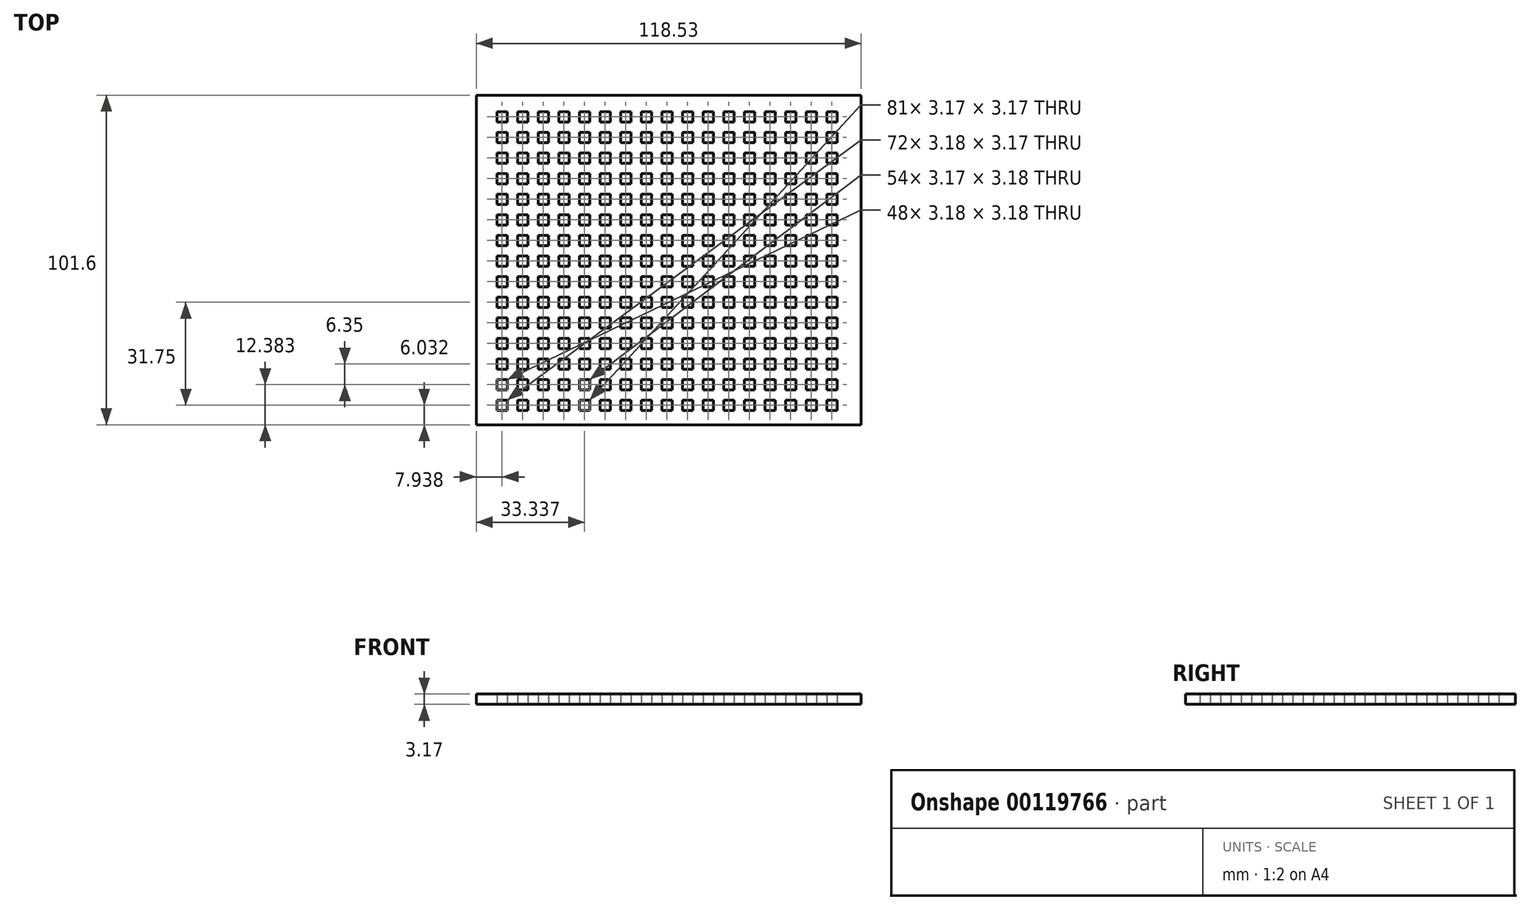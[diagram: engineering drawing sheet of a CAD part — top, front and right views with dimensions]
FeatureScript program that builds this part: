
annotation { "Feature Type Name" : "Feature", "Feature Type Description" : "" }
export const myFeature = defineFeature(function(context is Context, id is Id, definition is map)
    precondition{}
    {
        {
            assignVariable(context, id + "F0", {"name" : "thickness", "anyValue" : 3.17 * mm});
        }
        {
            var Q0;
            Q0=qCreatedBy(makeId("Top.planeOp"),FACE);
            var sketch = newSketch(context, id + "F1", { "sketchPlane" : qUnion([Q0])});
            skLineSegment(sketch, "E0.bottom", {"start": v(0, 0) * mm, "end": v(118.53, 0) * mm});
            skLineSegment(sketch, "E0.top", {"start": v(0, 101.6) * mm, "end": v(118.53, 101.6) * mm});
            skLineSegment(sketch, "E0.left", {"start": v(0, 0) * mm, "end": v(0, 101.6) * mm});
            skLineSegment(sketch, "E0.right", {"start": v(118.53, 0) * mm, "end": v(118.53, 101.6) * mm});
            skLineSegment(sketch, "E1.bottom", {"start": v(6.35, 93.35) * mm, "end": v(9.53, 93.35) * mm});
            skLineSegment(sketch, "E1.top", {"start": v(6.35, 96.52) * mm, "end": v(9.53, 96.52) * mm});
            skLineSegment(sketch, "E1.left", {"start": v(6.35, 93.35) * mm, "end": v(6.35, 96.52) * mm});
            skLineSegment(sketch, "E1.right", {"start": v(9.52, 93.35) * mm, "end": v(9.52, 96.52) * mm});
            skLineSegment(sketch, "E2.0.1.0", {"start": v(6.35, 90.17) * mm, "end": v(9.53, 90.17) * mm});
            skLineSegment(sketch, "E2.0.1.1", {"start": v(9.52, 87) * mm, "end": v(9.52, 90.17) * mm});
            skLineSegment(sketch, "E2.0.1.2", {"start": v(6.35, 87) * mm, "end": v(9.53, 87) * mm});
            skLineSegment(sketch, "E2.0.1.3", {"start": v(6.35, 87) * mm, "end": v(6.35, 90.17) * mm});
            skLineSegment(sketch, "E2.0.2.0", {"start": v(6.35, 83.82) * mm, "end": v(9.53, 83.82) * mm});
            skLineSegment(sketch, "E2.0.2.1", {"start": v(9.52, 80.65) * mm, "end": v(9.52, 83.82) * mm});
            skLineSegment(sketch, "E2.0.2.2", {"start": v(6.35, 80.65) * mm, "end": v(9.53, 80.65) * mm});
            skLineSegment(sketch, "E2.0.2.3", {"start": v(6.35, 80.65) * mm, "end": v(6.35, 83.82) * mm});
            skLineSegment(sketch, "E2.0.3.0", {"start": v(6.35, 77.47) * mm, "end": v(9.53, 77.47) * mm});
            skLineSegment(sketch, "E2.0.3.1", {"start": v(9.52, 74.3) * mm, "end": v(9.52, 77.47) * mm});
            skLineSegment(sketch, "E2.0.3.2", {"start": v(6.35, 74.3) * mm, "end": v(9.53, 74.3) * mm});
            skLineSegment(sketch, "E2.0.3.3", {"start": v(6.35, 74.3) * mm, "end": v(6.35, 77.47) * mm});
            skLineSegment(sketch, "E2.0.4.0", {"start": v(6.35, 71.12) * mm, "end": v(9.53, 71.12) * mm});
            skLineSegment(sketch, "E2.0.4.1", {"start": v(9.52, 67.95) * mm, "end": v(9.52, 71.12) * mm});
            skLineSegment(sketch, "E2.0.4.2", {"start": v(6.35, 67.95) * mm, "end": v(9.53, 67.95) * mm});
            skLineSegment(sketch, "E2.0.4.3", {"start": v(6.35, 67.95) * mm, "end": v(6.35, 71.12) * mm});
            skLineSegment(sketch, "E2.0.5.0", {"start": v(6.35, 64.77) * mm, "end": v(9.53, 64.77) * mm});
            skLineSegment(sketch, "E2.0.5.1", {"start": v(9.52, 61.6) * mm, "end": v(9.52, 64.77) * mm});
            skLineSegment(sketch, "E2.0.5.2", {"start": v(6.35, 61.6) * mm, "end": v(9.53, 61.6) * mm});
            skLineSegment(sketch, "E2.0.5.3", {"start": v(6.35, 61.6) * mm, "end": v(6.35, 64.77) * mm});
            skLineSegment(sketch, "E2.0.6.0", {"start": v(6.35, 58.42) * mm, "end": v(9.53, 58.42) * mm});
            skLineSegment(sketch, "E2.0.6.1", {"start": v(9.52, 55.25) * mm, "end": v(9.52, 58.42) * mm});
            skLineSegment(sketch, "E2.0.6.2", {"start": v(6.35, 55.25) * mm, "end": v(9.53, 55.25) * mm});
            skLineSegment(sketch, "E2.0.6.3", {"start": v(6.35, 55.25) * mm, "end": v(6.35, 58.42) * mm});
            skLineSegment(sketch, "E2.0.7.0", {"start": v(6.35, 52.07) * mm, "end": v(9.53, 52.07) * mm});
            skLineSegment(sketch, "E2.0.7.1", {"start": v(9.52, 48.9) * mm, "end": v(9.52, 52.07) * mm});
            skLineSegment(sketch, "E2.0.7.2", {"start": v(6.35, 48.9) * mm, "end": v(9.53, 48.9) * mm});
            skLineSegment(sketch, "E2.0.7.3", {"start": v(6.35, 48.9) * mm, "end": v(6.35, 52.07) * mm});
            skLineSegment(sketch, "E2.0.8.0", {"start": v(6.35, 45.72) * mm, "end": v(9.53, 45.72) * mm});
            skLineSegment(sketch, "E2.0.8.1", {"start": v(9.52, 42.55) * mm, "end": v(9.52, 45.72) * mm});
            skLineSegment(sketch, "E2.0.8.2", {"start": v(6.35, 42.55) * mm, "end": v(9.53, 42.55) * mm});
            skLineSegment(sketch, "E2.0.8.3", {"start": v(6.35, 42.55) * mm, "end": v(6.35, 45.72) * mm});
            skLineSegment(sketch, "E2.0.9.0", {"start": v(6.35, 39.37) * mm, "end": v(9.53, 39.37) * mm});
            skLineSegment(sketch, "E2.0.9.1", {"start": v(9.52, 36.2) * mm, "end": v(9.52, 39.37) * mm});
            skLineSegment(sketch, "E2.0.9.2", {"start": v(6.35, 36.2) * mm, "end": v(9.53, 36.2) * mm});
            skLineSegment(sketch, "E2.0.9.3", {"start": v(6.35, 36.2) * mm, "end": v(6.35, 39.37) * mm});
            skLineSegment(sketch, "E2.0.10.0", {"start": v(6.35, 33.02) * mm, "end": v(9.53, 33.02) * mm});
            skLineSegment(sketch, "E2.0.10.1", {"start": v(9.52, 29.85) * mm, "end": v(9.52, 33.02) * mm});
            skLineSegment(sketch, "E2.0.10.2", {"start": v(6.35, 29.85) * mm, "end": v(9.53, 29.85) * mm});
            skLineSegment(sketch, "E2.0.10.3", {"start": v(6.35, 29.85) * mm, "end": v(6.35, 33.02) * mm});
            skLineSegment(sketch, "E2.0.11.0", {"start": v(6.35, 26.67) * mm, "end": v(9.53, 26.67) * mm});
            skLineSegment(sketch, "E2.0.11.1", {"start": v(9.52, 23.5) * mm, "end": v(9.52, 26.67) * mm});
            skLineSegment(sketch, "E2.0.11.2", {"start": v(6.35, 23.5) * mm, "end": v(9.53, 23.5) * mm});
            skLineSegment(sketch, "E2.0.11.3", {"start": v(6.35, 23.5) * mm, "end": v(6.35, 26.67) * mm});
            skLineSegment(sketch, "E2.0.12.0", {"start": v(6.35, 20.32) * mm, "end": v(9.53, 20.32) * mm});
            skLineSegment(sketch, "E2.0.12.1", {"start": v(9.52, 17.15) * mm, "end": v(9.52, 20.32) * mm});
            skLineSegment(sketch, "E2.0.12.2", {"start": v(6.35, 17.15) * mm, "end": v(9.53, 17.15) * mm});
            skLineSegment(sketch, "E2.0.12.3", {"start": v(6.35, 17.15) * mm, "end": v(6.35, 20.32) * mm});
            skLineSegment(sketch, "E2.0.13.0", {"start": v(6.35, 13.97) * mm, "end": v(9.53, 13.97) * mm});
            skLineSegment(sketch, "E2.0.13.1", {"start": v(9.52, 10.8) * mm, "end": v(9.52, 13.97) * mm});
            skLineSegment(sketch, "E2.0.13.2", {"start": v(6.35, 10.8) * mm, "end": v(9.53, 10.8) * mm});
            skLineSegment(sketch, "E2.0.13.3", {"start": v(6.35, 10.8) * mm, "end": v(6.35, 13.97) * mm});
            skLineSegment(sketch, "E2.0.14.0", {"start": v(6.35, 7.62) * mm, "end": v(9.53, 7.62) * mm});
            skLineSegment(sketch, "E2.0.14.1", {"start": v(9.52, 4.45) * mm, "end": v(9.52, 7.62) * mm});
            skLineSegment(sketch, "E2.0.14.2", {"start": v(6.35, 4.45) * mm, "end": v(9.53, 4.45) * mm});
            skLineSegment(sketch, "E2.0.14.3", {"start": v(6.35, 4.45) * mm, "end": v(6.35, 7.62) * mm});
            skLineSegment(sketch, "E2.1.0.0", {"start": v(12.7, 96.52) * mm, "end": v(15.87, 96.52) * mm});
            skLineSegment(sketch, "E2.1.0.1", {"start": v(15.87, 93.35) * mm, "end": v(15.87, 96.52) * mm});
            skLineSegment(sketch, "E2.1.0.2", {"start": v(12.7, 93.35) * mm, "end": v(15.87, 93.35) * mm});
            skLineSegment(sketch, "E2.1.0.3", {"start": v(12.7, 93.35) * mm, "end": v(12.7, 96.52) * mm});
            skLineSegment(sketch, "E2.1.1.0", {"start": v(12.7, 90.17) * mm, "end": v(15.87, 90.17) * mm});
            skLineSegment(sketch, "E2.1.1.1", {"start": v(15.87, 87) * mm, "end": v(15.87, 90.17) * mm});
            skLineSegment(sketch, "E2.1.1.2", {"start": v(12.7, 87) * mm, "end": v(15.87, 87) * mm});
            skLineSegment(sketch, "E2.1.1.3", {"start": v(12.7, 87) * mm, "end": v(12.7, 90.17) * mm});
            skLineSegment(sketch, "E2.1.2.0", {"start": v(12.7, 83.82) * mm, "end": v(15.87, 83.82) * mm});
            skLineSegment(sketch, "E2.1.2.1", {"start": v(15.87, 80.65) * mm, "end": v(15.87, 83.82) * mm});
            skLineSegment(sketch, "E2.1.2.2", {"start": v(12.7, 80.65) * mm, "end": v(15.87, 80.65) * mm});
            skLineSegment(sketch, "E2.1.2.3", {"start": v(12.7, 80.65) * mm, "end": v(12.7, 83.82) * mm});
            skLineSegment(sketch, "E2.1.3.0", {"start": v(12.7, 77.47) * mm, "end": v(15.87, 77.47) * mm});
            skLineSegment(sketch, "E2.1.3.1", {"start": v(15.87, 74.3) * mm, "end": v(15.87, 77.47) * mm});
            skLineSegment(sketch, "E2.1.3.2", {"start": v(12.7, 74.3) * mm, "end": v(15.87, 74.3) * mm});
            skLineSegment(sketch, "E2.1.3.3", {"start": v(12.7, 74.3) * mm, "end": v(12.7, 77.47) * mm});
            skLineSegment(sketch, "E2.1.4.0", {"start": v(12.7, 71.12) * mm, "end": v(15.87, 71.12) * mm});
            skLineSegment(sketch, "E2.1.4.1", {"start": v(15.87, 67.95) * mm, "end": v(15.87, 71.12) * mm});
            skLineSegment(sketch, "E2.1.4.2", {"start": v(12.7, 67.95) * mm, "end": v(15.87, 67.95) * mm});
            skLineSegment(sketch, "E2.1.4.3", {"start": v(12.7, 67.95) * mm, "end": v(12.7, 71.12) * mm});
            skLineSegment(sketch, "E2.1.5.0", {"start": v(12.7, 64.77) * mm, "end": v(15.87, 64.77) * mm});
            skLineSegment(sketch, "E2.1.5.1", {"start": v(15.87, 61.6) * mm, "end": v(15.87, 64.77) * mm});
            skLineSegment(sketch, "E2.1.5.2", {"start": v(12.7, 61.6) * mm, "end": v(15.87, 61.6) * mm});
            skLineSegment(sketch, "E2.1.5.3", {"start": v(12.7, 61.6) * mm, "end": v(12.7, 64.77) * mm});
            skLineSegment(sketch, "E2.1.6.0", {"start": v(12.7, 58.42) * mm, "end": v(15.87, 58.42) * mm});
            skLineSegment(sketch, "E2.1.6.1", {"start": v(15.87, 55.25) * mm, "end": v(15.87, 58.42) * mm});
            skLineSegment(sketch, "E2.1.6.2", {"start": v(12.7, 55.25) * mm, "end": v(15.87, 55.25) * mm});
            skLineSegment(sketch, "E2.1.6.3", {"start": v(12.7, 55.25) * mm, "end": v(12.7, 58.42) * mm});
            skLineSegment(sketch, "E2.1.7.0", {"start": v(12.7, 52.07) * mm, "end": v(15.87, 52.07) * mm});
            skLineSegment(sketch, "E2.1.7.1", {"start": v(15.87, 48.9) * mm, "end": v(15.87, 52.07) * mm});
            skLineSegment(sketch, "E2.1.7.2", {"start": v(12.7, 48.9) * mm, "end": v(15.87, 48.9) * mm});
            skLineSegment(sketch, "E2.1.7.3", {"start": v(12.7, 48.9) * mm, "end": v(12.7, 52.07) * mm});
            skLineSegment(sketch, "E2.1.8.0", {"start": v(12.7, 45.72) * mm, "end": v(15.87, 45.72) * mm});
            skLineSegment(sketch, "E2.1.8.1", {"start": v(15.87, 42.55) * mm, "end": v(15.87, 45.72) * mm});
            skLineSegment(sketch, "E2.1.8.2", {"start": v(12.7, 42.55) * mm, "end": v(15.87, 42.55) * mm});
            skLineSegment(sketch, "E2.1.8.3", {"start": v(12.7, 42.55) * mm, "end": v(12.7, 45.72) * mm});
            skLineSegment(sketch, "E2.1.9.0", {"start": v(12.7, 39.37) * mm, "end": v(15.87, 39.37) * mm});
            skLineSegment(sketch, "E2.1.9.1", {"start": v(15.87, 36.2) * mm, "end": v(15.87, 39.37) * mm});
            skLineSegment(sketch, "E2.1.9.2", {"start": v(12.7, 36.2) * mm, "end": v(15.87, 36.2) * mm});
            skLineSegment(sketch, "E2.1.9.3", {"start": v(12.7, 36.2) * mm, "end": v(12.7, 39.37) * mm});
            skLineSegment(sketch, "E2.1.10.0", {"start": v(12.7, 33.02) * mm, "end": v(15.87, 33.02) * mm});
            skLineSegment(sketch, "E2.1.10.1", {"start": v(15.87, 29.85) * mm, "end": v(15.87, 33.02) * mm});
            skLineSegment(sketch, "E2.1.10.2", {"start": v(12.7, 29.85) * mm, "end": v(15.87, 29.85) * mm});
            skLineSegment(sketch, "E2.1.10.3", {"start": v(12.7, 29.85) * mm, "end": v(12.7, 33.02) * mm});
            skLineSegment(sketch, "E2.1.11.0", {"start": v(12.7, 26.67) * mm, "end": v(15.87, 26.67) * mm});
            skLineSegment(sketch, "E2.1.11.1", {"start": v(15.87, 23.5) * mm, "end": v(15.87, 26.67) * mm});
            skLineSegment(sketch, "E2.1.11.2", {"start": v(12.7, 23.5) * mm, "end": v(15.87, 23.5) * mm});
            skLineSegment(sketch, "E2.1.11.3", {"start": v(12.7, 23.5) * mm, "end": v(12.7, 26.67) * mm});
            skLineSegment(sketch, "E2.1.12.0", {"start": v(12.7, 20.32) * mm, "end": v(15.87, 20.32) * mm});
            skLineSegment(sketch, "E2.1.12.1", {"start": v(15.87, 17.15) * mm, "end": v(15.87, 20.32) * mm});
            skLineSegment(sketch, "E2.1.12.2", {"start": v(12.7, 17.15) * mm, "end": v(15.87, 17.15) * mm});
            skLineSegment(sketch, "E2.1.12.3", {"start": v(12.7, 17.15) * mm, "end": v(12.7, 20.32) * mm});
            skLineSegment(sketch, "E2.1.13.0", {"start": v(12.7, 13.97) * mm, "end": v(15.87, 13.97) * mm});
            skLineSegment(sketch, "E2.1.13.1", {"start": v(15.87, 10.8) * mm, "end": v(15.87, 13.97) * mm});
            skLineSegment(sketch, "E2.1.13.2", {"start": v(12.7, 10.8) * mm, "end": v(15.87, 10.8) * mm});
            skLineSegment(sketch, "E2.1.13.3", {"start": v(12.7, 10.8) * mm, "end": v(12.7, 13.97) * mm});
            skLineSegment(sketch, "E2.1.14.0", {"start": v(12.7, 7.62) * mm, "end": v(15.87, 7.62) * mm});
            skLineSegment(sketch, "E2.1.14.1", {"start": v(15.87, 4.45) * mm, "end": v(15.87, 7.62) * mm});
            skLineSegment(sketch, "E2.1.14.2", {"start": v(12.7, 4.45) * mm, "end": v(15.87, 4.45) * mm});
            skLineSegment(sketch, "E2.1.14.3", {"start": v(12.7, 4.45) * mm, "end": v(12.7, 7.62) * mm});
            skLineSegment(sketch, "E2.2.0.0", {"start": v(19.05, 96.52) * mm, "end": v(22.22, 96.52) * mm});
            skLineSegment(sketch, "E2.2.0.1", {"start": v(22.22, 93.35) * mm, "end": v(22.22, 96.52) * mm});
            skLineSegment(sketch, "E2.2.0.2", {"start": v(19.05, 93.35) * mm, "end": v(22.22, 93.35) * mm});
            skLineSegment(sketch, "E2.2.0.3", {"start": v(19.05, 93.35) * mm, "end": v(19.05, 96.52) * mm});
            skLineSegment(sketch, "E2.2.1.0", {"start": v(19.05, 90.17) * mm, "end": v(22.22, 90.17) * mm});
            skLineSegment(sketch, "E2.2.1.1", {"start": v(22.22, 87) * mm, "end": v(22.22, 90.17) * mm});
            skLineSegment(sketch, "E2.2.1.2", {"start": v(19.05, 87) * mm, "end": v(22.22, 87) * mm});
            skLineSegment(sketch, "E2.2.1.3", {"start": v(19.05, 87) * mm, "end": v(19.05, 90.17) * mm});
            skLineSegment(sketch, "E2.2.2.0", {"start": v(19.05, 83.82) * mm, "end": v(22.22, 83.82) * mm});
            skLineSegment(sketch, "E2.2.2.1", {"start": v(22.22, 80.65) * mm, "end": v(22.22, 83.82) * mm});
            skLineSegment(sketch, "E2.2.2.2", {"start": v(19.05, 80.65) * mm, "end": v(22.22, 80.65) * mm});
            skLineSegment(sketch, "E2.2.2.3", {"start": v(19.05, 80.65) * mm, "end": v(19.05, 83.82) * mm});
            skLineSegment(sketch, "E2.2.3.0", {"start": v(19.05, 77.47) * mm, "end": v(22.22, 77.47) * mm});
            skLineSegment(sketch, "E2.2.3.1", {"start": v(22.22, 74.3) * mm, "end": v(22.22, 77.47) * mm});
            skLineSegment(sketch, "E2.2.3.2", {"start": v(19.05, 74.3) * mm, "end": v(22.22, 74.3) * mm});
            skLineSegment(sketch, "E2.2.3.3", {"start": v(19.05, 74.3) * mm, "end": v(19.05, 77.47) * mm});
            skLineSegment(sketch, "E2.2.4.0", {"start": v(19.05, 71.12) * mm, "end": v(22.22, 71.12) * mm});
            skLineSegment(sketch, "E2.2.4.1", {"start": v(22.22, 67.95) * mm, "end": v(22.22, 71.12) * mm});
            skLineSegment(sketch, "E2.2.4.2", {"start": v(19.05, 67.95) * mm, "end": v(22.22, 67.95) * mm});
            skLineSegment(sketch, "E2.2.4.3", {"start": v(19.05, 67.95) * mm, "end": v(19.05, 71.12) * mm});
            skLineSegment(sketch, "E2.2.5.0", {"start": v(19.05, 64.77) * mm, "end": v(22.22, 64.77) * mm});
            skLineSegment(sketch, "E2.2.5.1", {"start": v(22.22, 61.6) * mm, "end": v(22.22, 64.77) * mm});
            skLineSegment(sketch, "E2.2.5.2", {"start": v(19.05, 61.6) * mm, "end": v(22.22, 61.6) * mm});
            skLineSegment(sketch, "E2.2.5.3", {"start": v(19.05, 61.6) * mm, "end": v(19.05, 64.77) * mm});
            skLineSegment(sketch, "E2.2.6.0", {"start": v(19.05, 58.42) * mm, "end": v(22.22, 58.42) * mm});
            skLineSegment(sketch, "E2.2.6.1", {"start": v(22.22, 55.25) * mm, "end": v(22.22, 58.42) * mm});
            skLineSegment(sketch, "E2.2.6.2", {"start": v(19.05, 55.25) * mm, "end": v(22.22, 55.25) * mm});
            skLineSegment(sketch, "E2.2.6.3", {"start": v(19.05, 55.25) * mm, "end": v(19.05, 58.42) * mm});
            skLineSegment(sketch, "E2.2.7.0", {"start": v(19.05, 52.07) * mm, "end": v(22.22, 52.07) * mm});
            skLineSegment(sketch, "E2.2.7.1", {"start": v(22.22, 48.9) * mm, "end": v(22.22, 52.07) * mm});
            skLineSegment(sketch, "E2.2.7.2", {"start": v(19.05, 48.9) * mm, "end": v(22.22, 48.9) * mm});
            skLineSegment(sketch, "E2.2.7.3", {"start": v(19.05, 48.9) * mm, "end": v(19.05, 52.07) * mm});
            skLineSegment(sketch, "E2.2.8.0", {"start": v(19.05, 45.72) * mm, "end": v(22.22, 45.72) * mm});
            skLineSegment(sketch, "E2.2.8.1", {"start": v(22.22, 42.55) * mm, "end": v(22.22, 45.72) * mm});
            skLineSegment(sketch, "E2.2.8.2", {"start": v(19.05, 42.55) * mm, "end": v(22.22, 42.55) * mm});
            skLineSegment(sketch, "E2.2.8.3", {"start": v(19.05, 42.55) * mm, "end": v(19.05, 45.72) * mm});
            skLineSegment(sketch, "E2.2.9.0", {"start": v(19.05, 39.37) * mm, "end": v(22.22, 39.37) * mm});
            skLineSegment(sketch, "E2.2.9.1", {"start": v(22.22, 36.2) * mm, "end": v(22.22, 39.37) * mm});
            skLineSegment(sketch, "E2.2.9.2", {"start": v(19.05, 36.2) * mm, "end": v(22.22, 36.2) * mm});
            skLineSegment(sketch, "E2.2.9.3", {"start": v(19.05, 36.2) * mm, "end": v(19.05, 39.37) * mm});
            skLineSegment(sketch, "E2.2.10.0", {"start": v(19.05, 33.02) * mm, "end": v(22.22, 33.02) * mm});
            skLineSegment(sketch, "E2.2.10.1", {"start": v(22.22, 29.85) * mm, "end": v(22.22, 33.02) * mm});
            skLineSegment(sketch, "E2.2.10.2", {"start": v(19.05, 29.85) * mm, "end": v(22.22, 29.85) * mm});
            skLineSegment(sketch, "E2.2.10.3", {"start": v(19.05, 29.85) * mm, "end": v(19.05, 33.02) * mm});
            skLineSegment(sketch, "E2.2.11.0", {"start": v(19.05, 26.67) * mm, "end": v(22.22, 26.67) * mm});
            skLineSegment(sketch, "E2.2.11.1", {"start": v(22.22, 23.5) * mm, "end": v(22.22, 26.67) * mm});
            skLineSegment(sketch, "E2.2.11.2", {"start": v(19.05, 23.5) * mm, "end": v(22.22, 23.5) * mm});
            skLineSegment(sketch, "E2.2.11.3", {"start": v(19.05, 23.5) * mm, "end": v(19.05, 26.67) * mm});
            skLineSegment(sketch, "E2.2.12.0", {"start": v(19.05, 20.32) * mm, "end": v(22.22, 20.32) * mm});
            skLineSegment(sketch, "E2.2.12.1", {"start": v(22.22, 17.15) * mm, "end": v(22.22, 20.32) * mm});
            skLineSegment(sketch, "E2.2.12.2", {"start": v(19.05, 17.15) * mm, "end": v(22.22, 17.15) * mm});
            skLineSegment(sketch, "E2.2.12.3", {"start": v(19.05, 17.15) * mm, "end": v(19.05, 20.32) * mm});
            skLineSegment(sketch, "E2.2.13.0", {"start": v(19.05, 13.97) * mm, "end": v(22.22, 13.97) * mm});
            skLineSegment(sketch, "E2.2.13.1", {"start": v(22.22, 10.8) * mm, "end": v(22.22, 13.97) * mm});
            skLineSegment(sketch, "E2.2.13.2", {"start": v(19.05, 10.8) * mm, "end": v(22.22, 10.8) * mm});
            skLineSegment(sketch, "E2.2.13.3", {"start": v(19.05, 10.8) * mm, "end": v(19.05, 13.97) * mm});
            skLineSegment(sketch, "E2.2.14.0", {"start": v(19.05, 7.62) * mm, "end": v(22.22, 7.62) * mm});
            skLineSegment(sketch, "E2.2.14.1", {"start": v(22.22, 4.45) * mm, "end": v(22.22, 7.62) * mm});
            skLineSegment(sketch, "E2.2.14.2", {"start": v(19.05, 4.45) * mm, "end": v(22.22, 4.45) * mm});
            skLineSegment(sketch, "E2.2.14.3", {"start": v(19.05, 4.45) * mm, "end": v(19.05, 7.62) * mm});
            skLineSegment(sketch, "E2.3.0.0", {"start": v(25.4, 96.52) * mm, "end": v(28.57, 96.52) * mm});
            skLineSegment(sketch, "E2.3.0.1", {"start": v(28.57, 93.35) * mm, "end": v(28.57, 96.52) * mm});
            skLineSegment(sketch, "E2.3.0.2", {"start": v(25.4, 93.35) * mm, "end": v(28.57, 93.35) * mm});
            skLineSegment(sketch, "E2.3.0.3", {"start": v(25.4, 93.35) * mm, "end": v(25.4, 96.52) * mm});
            skLineSegment(sketch, "E2.3.1.0", {"start": v(25.4, 90.17) * mm, "end": v(28.57, 90.17) * mm});
            skLineSegment(sketch, "E2.3.1.1", {"start": v(28.57, 87) * mm, "end": v(28.57, 90.17) * mm});
            skLineSegment(sketch, "E2.3.1.2", {"start": v(25.4, 87) * mm, "end": v(28.57, 87) * mm});
            skLineSegment(sketch, "E2.3.1.3", {"start": v(25.4, 87) * mm, "end": v(25.4, 90.17) * mm});
            skLineSegment(sketch, "E2.3.2.0", {"start": v(25.4, 83.82) * mm, "end": v(28.57, 83.82) * mm});
            skLineSegment(sketch, "E2.3.2.1", {"start": v(28.57, 80.65) * mm, "end": v(28.57, 83.82) * mm});
            skLineSegment(sketch, "E2.3.2.2", {"start": v(25.4, 80.65) * mm, "end": v(28.57, 80.65) * mm});
            skLineSegment(sketch, "E2.3.2.3", {"start": v(25.4, 80.65) * mm, "end": v(25.4, 83.82) * mm});
            skLineSegment(sketch, "E2.3.3.0", {"start": v(25.4, 77.47) * mm, "end": v(28.57, 77.47) * mm});
            skLineSegment(sketch, "E2.3.3.1", {"start": v(28.57, 74.3) * mm, "end": v(28.57, 77.47) * mm});
            skLineSegment(sketch, "E2.3.3.2", {"start": v(25.4, 74.3) * mm, "end": v(28.57, 74.3) * mm});
            skLineSegment(sketch, "E2.3.3.3", {"start": v(25.4, 74.3) * mm, "end": v(25.4, 77.47) * mm});
            skLineSegment(sketch, "E2.3.4.0", {"start": v(25.4, 71.12) * mm, "end": v(28.57, 71.12) * mm});
            skLineSegment(sketch, "E2.3.4.1", {"start": v(28.57, 67.95) * mm, "end": v(28.57, 71.12) * mm});
            skLineSegment(sketch, "E2.3.4.2", {"start": v(25.4, 67.95) * mm, "end": v(28.57, 67.95) * mm});
            skLineSegment(sketch, "E2.3.4.3", {"start": v(25.4, 67.95) * mm, "end": v(25.4, 71.12) * mm});
            skLineSegment(sketch, "E2.3.5.0", {"start": v(25.4, 64.77) * mm, "end": v(28.57, 64.77) * mm});
            skLineSegment(sketch, "E2.3.5.1", {"start": v(28.57, 61.6) * mm, "end": v(28.57, 64.77) * mm});
            skLineSegment(sketch, "E2.3.5.2", {"start": v(25.4, 61.6) * mm, "end": v(28.57, 61.6) * mm});
            skLineSegment(sketch, "E2.3.5.3", {"start": v(25.4, 61.6) * mm, "end": v(25.4, 64.77) * mm});
            skLineSegment(sketch, "E2.3.6.0", {"start": v(25.4, 58.42) * mm, "end": v(28.57, 58.42) * mm});
            skLineSegment(sketch, "E2.3.6.1", {"start": v(28.57, 55.25) * mm, "end": v(28.57, 58.42) * mm});
            skLineSegment(sketch, "E2.3.6.2", {"start": v(25.4, 55.25) * mm, "end": v(28.57, 55.25) * mm});
            skLineSegment(sketch, "E2.3.6.3", {"start": v(25.4, 55.25) * mm, "end": v(25.4, 58.42) * mm});
            skLineSegment(sketch, "E2.3.7.0", {"start": v(25.4, 52.07) * mm, "end": v(28.57, 52.07) * mm});
            skLineSegment(sketch, "E2.3.7.1", {"start": v(28.57, 48.9) * mm, "end": v(28.57, 52.07) * mm});
            skLineSegment(sketch, "E2.3.7.2", {"start": v(25.4, 48.9) * mm, "end": v(28.57, 48.9) * mm});
            skLineSegment(sketch, "E2.3.7.3", {"start": v(25.4, 48.9) * mm, "end": v(25.4, 52.07) * mm});
            skLineSegment(sketch, "E2.3.8.0", {"start": v(25.4, 45.72) * mm, "end": v(28.57, 45.72) * mm});
            skLineSegment(sketch, "E2.3.8.1", {"start": v(28.57, 42.55) * mm, "end": v(28.57, 45.72) * mm});
            skLineSegment(sketch, "E2.3.8.2", {"start": v(25.4, 42.55) * mm, "end": v(28.57, 42.55) * mm});
            skLineSegment(sketch, "E2.3.8.3", {"start": v(25.4, 42.55) * mm, "end": v(25.4, 45.72) * mm});
            skLineSegment(sketch, "E2.3.9.0", {"start": v(25.4, 39.37) * mm, "end": v(28.57, 39.37) * mm});
            skLineSegment(sketch, "E2.3.9.1", {"start": v(28.57, 36.2) * mm, "end": v(28.57, 39.37) * mm});
            skLineSegment(sketch, "E2.3.9.2", {"start": v(25.4, 36.2) * mm, "end": v(28.57, 36.2) * mm});
            skLineSegment(sketch, "E2.3.9.3", {"start": v(25.4, 36.2) * mm, "end": v(25.4, 39.37) * mm});
            skLineSegment(sketch, "E2.3.10.0", {"start": v(25.4, 33.02) * mm, "end": v(28.57, 33.02) * mm});
            skLineSegment(sketch, "E2.3.10.1", {"start": v(28.57, 29.85) * mm, "end": v(28.57, 33.02) * mm});
            skLineSegment(sketch, "E2.3.10.2", {"start": v(25.4, 29.85) * mm, "end": v(28.57, 29.85) * mm});
            skLineSegment(sketch, "E2.3.10.3", {"start": v(25.4, 29.85) * mm, "end": v(25.4, 33.02) * mm});
            skLineSegment(sketch, "E2.3.11.0", {"start": v(25.4, 26.67) * mm, "end": v(28.57, 26.67) * mm});
            skLineSegment(sketch, "E2.3.11.1", {"start": v(28.57, 23.5) * mm, "end": v(28.57, 26.67) * mm});
            skLineSegment(sketch, "E2.3.11.2", {"start": v(25.4, 23.5) * mm, "end": v(28.57, 23.5) * mm});
            skLineSegment(sketch, "E2.3.11.3", {"start": v(25.4, 23.5) * mm, "end": v(25.4, 26.67) * mm});
            skLineSegment(sketch, "E2.3.12.0", {"start": v(25.4, 20.32) * mm, "end": v(28.57, 20.32) * mm});
            skLineSegment(sketch, "E2.3.12.1", {"start": v(28.57, 17.15) * mm, "end": v(28.57, 20.32) * mm});
            skLineSegment(sketch, "E2.3.12.2", {"start": v(25.4, 17.15) * mm, "end": v(28.57, 17.15) * mm});
            skLineSegment(sketch, "E2.3.12.3", {"start": v(25.4, 17.15) * mm, "end": v(25.4, 20.32) * mm});
            skLineSegment(sketch, "E2.3.13.0", {"start": v(25.4, 13.97) * mm, "end": v(28.57, 13.97) * mm});
            skLineSegment(sketch, "E2.3.13.1", {"start": v(28.57, 10.8) * mm, "end": v(28.57, 13.97) * mm});
            skLineSegment(sketch, "E2.3.13.2", {"start": v(25.4, 10.8) * mm, "end": v(28.57, 10.8) * mm});
            skLineSegment(sketch, "E2.3.13.3", {"start": v(25.4, 10.8) * mm, "end": v(25.4, 13.97) * mm});
            skLineSegment(sketch, "E2.3.14.0", {"start": v(25.4, 7.62) * mm, "end": v(28.57, 7.62) * mm});
            skLineSegment(sketch, "E2.3.14.1", {"start": v(28.57, 4.45) * mm, "end": v(28.57, 7.62) * mm});
            skLineSegment(sketch, "E2.3.14.2", {"start": v(25.4, 4.45) * mm, "end": v(28.57, 4.45) * mm});
            skLineSegment(sketch, "E2.3.14.3", {"start": v(25.4, 4.45) * mm, "end": v(25.4, 7.62) * mm});
            skLineSegment(sketch, "E2.4.0.0", {"start": v(31.75, 96.52) * mm, "end": v(34.92, 96.52) * mm});
            skLineSegment(sketch, "E2.4.0.1", {"start": v(34.92, 93.35) * mm, "end": v(34.92, 96.52) * mm});
            skLineSegment(sketch, "E2.4.0.2", {"start": v(31.75, 93.35) * mm, "end": v(34.92, 93.35) * mm});
            skLineSegment(sketch, "E2.4.0.3", {"start": v(31.75, 93.35) * mm, "end": v(31.75, 96.52) * mm});
            skLineSegment(sketch, "E2.4.1.0", {"start": v(31.75, 90.17) * mm, "end": v(34.92, 90.17) * mm});
            skLineSegment(sketch, "E2.4.1.1", {"start": v(34.92, 87) * mm, "end": v(34.92, 90.17) * mm});
            skLineSegment(sketch, "E2.4.1.2", {"start": v(31.75, 87) * mm, "end": v(34.92, 87) * mm});
            skLineSegment(sketch, "E2.4.1.3", {"start": v(31.75, 87) * mm, "end": v(31.75, 90.17) * mm});
            skLineSegment(sketch, "E2.4.2.0", {"start": v(31.75, 83.82) * mm, "end": v(34.92, 83.82) * mm});
            skLineSegment(sketch, "E2.4.2.1", {"start": v(34.92, 80.65) * mm, "end": v(34.92, 83.82) * mm});
            skLineSegment(sketch, "E2.4.2.2", {"start": v(31.75, 80.65) * mm, "end": v(34.92, 80.65) * mm});
            skLineSegment(sketch, "E2.4.2.3", {"start": v(31.75, 80.65) * mm, "end": v(31.75, 83.82) * mm});
            skLineSegment(sketch, "E2.4.3.0", {"start": v(31.75, 77.47) * mm, "end": v(34.92, 77.47) * mm});
            skLineSegment(sketch, "E2.4.3.1", {"start": v(34.92, 74.3) * mm, "end": v(34.92, 77.47) * mm});
            skLineSegment(sketch, "E2.4.3.2", {"start": v(31.75, 74.3) * mm, "end": v(34.92, 74.3) * mm});
            skLineSegment(sketch, "E2.4.3.3", {"start": v(31.75, 74.3) * mm, "end": v(31.75, 77.47) * mm});
            skLineSegment(sketch, "E2.4.4.0", {"start": v(31.75, 71.12) * mm, "end": v(34.92, 71.12) * mm});
            skLineSegment(sketch, "E2.4.4.1", {"start": v(34.92, 67.95) * mm, "end": v(34.92, 71.12) * mm});
            skLineSegment(sketch, "E2.4.4.2", {"start": v(31.75, 67.95) * mm, "end": v(34.92, 67.95) * mm});
            skLineSegment(sketch, "E2.4.4.3", {"start": v(31.75, 67.95) * mm, "end": v(31.75, 71.12) * mm});
            skLineSegment(sketch, "E2.4.5.0", {"start": v(31.75, 64.77) * mm, "end": v(34.92, 64.77) * mm});
            skLineSegment(sketch, "E2.4.5.1", {"start": v(34.92, 61.6) * mm, "end": v(34.92, 64.77) * mm});
            skLineSegment(sketch, "E2.4.5.2", {"start": v(31.75, 61.6) * mm, "end": v(34.92, 61.6) * mm});
            skLineSegment(sketch, "E2.4.5.3", {"start": v(31.75, 61.6) * mm, "end": v(31.75, 64.77) * mm});
            skLineSegment(sketch, "E2.4.6.0", {"start": v(31.75, 58.42) * mm, "end": v(34.92, 58.42) * mm});
            skLineSegment(sketch, "E2.4.6.1", {"start": v(34.92, 55.25) * mm, "end": v(34.92, 58.42) * mm});
            skLineSegment(sketch, "E2.4.6.2", {"start": v(31.75, 55.25) * mm, "end": v(34.92, 55.25) * mm});
            skLineSegment(sketch, "E2.4.6.3", {"start": v(31.75, 55.25) * mm, "end": v(31.75, 58.42) * mm});
            skLineSegment(sketch, "E2.4.7.0", {"start": v(31.75, 52.07) * mm, "end": v(34.92, 52.07) * mm});
            skLineSegment(sketch, "E2.4.7.1", {"start": v(34.92, 48.9) * mm, "end": v(34.92, 52.07) * mm});
            skLineSegment(sketch, "E2.4.7.2", {"start": v(31.75, 48.9) * mm, "end": v(34.92, 48.9) * mm});
            skLineSegment(sketch, "E2.4.7.3", {"start": v(31.75, 48.9) * mm, "end": v(31.75, 52.07) * mm});
            skLineSegment(sketch, "E2.4.8.0", {"start": v(31.75, 45.72) * mm, "end": v(34.92, 45.72) * mm});
            skLineSegment(sketch, "E2.4.8.1", {"start": v(34.92, 42.55) * mm, "end": v(34.92, 45.72) * mm});
            skLineSegment(sketch, "E2.4.8.2", {"start": v(31.75, 42.55) * mm, "end": v(34.92, 42.55) * mm});
            skLineSegment(sketch, "E2.4.8.3", {"start": v(31.75, 42.55) * mm, "end": v(31.75, 45.72) * mm});
            skLineSegment(sketch, "E2.4.9.0", {"start": v(31.75, 39.37) * mm, "end": v(34.92, 39.37) * mm});
            skLineSegment(sketch, "E2.4.9.1", {"start": v(34.92, 36.2) * mm, "end": v(34.92, 39.37) * mm});
            skLineSegment(sketch, "E2.4.9.2", {"start": v(31.75, 36.2) * mm, "end": v(34.92, 36.2) * mm});
            skLineSegment(sketch, "E2.4.9.3", {"start": v(31.75, 36.2) * mm, "end": v(31.75, 39.37) * mm});
            skLineSegment(sketch, "E2.4.10.0", {"start": v(31.75, 33.02) * mm, "end": v(34.92, 33.02) * mm});
            skLineSegment(sketch, "E2.4.10.1", {"start": v(34.92, 29.85) * mm, "end": v(34.92, 33.02) * mm});
            skLineSegment(sketch, "E2.4.10.2", {"start": v(31.75, 29.85) * mm, "end": v(34.92, 29.85) * mm});
            skLineSegment(sketch, "E2.4.10.3", {"start": v(31.75, 29.85) * mm, "end": v(31.75, 33.02) * mm});
            skLineSegment(sketch, "E2.4.11.0", {"start": v(31.75, 26.67) * mm, "end": v(34.92, 26.67) * mm});
            skLineSegment(sketch, "E2.4.11.1", {"start": v(34.92, 23.5) * mm, "end": v(34.92, 26.67) * mm});
            skLineSegment(sketch, "E2.4.11.2", {"start": v(31.75, 23.5) * mm, "end": v(34.92, 23.5) * mm});
            skLineSegment(sketch, "E2.4.11.3", {"start": v(31.75, 23.5) * mm, "end": v(31.75, 26.67) * mm});
            skLineSegment(sketch, "E2.4.12.0", {"start": v(31.75, 20.32) * mm, "end": v(34.92, 20.32) * mm});
            skLineSegment(sketch, "E2.4.12.1", {"start": v(34.92, 17.15) * mm, "end": v(34.92, 20.32) * mm});
            skLineSegment(sketch, "E2.4.12.2", {"start": v(31.75, 17.15) * mm, "end": v(34.92, 17.15) * mm});
            skLineSegment(sketch, "E2.4.12.3", {"start": v(31.75, 17.15) * mm, "end": v(31.75, 20.32) * mm});
            skLineSegment(sketch, "E2.4.13.0", {"start": v(31.75, 13.97) * mm, "end": v(34.92, 13.97) * mm});
            skLineSegment(sketch, "E2.4.13.1", {"start": v(34.92, 10.8) * mm, "end": v(34.92, 13.97) * mm});
            skLineSegment(sketch, "E2.4.13.2", {"start": v(31.75, 10.8) * mm, "end": v(34.92, 10.8) * mm});
            skLineSegment(sketch, "E2.4.13.3", {"start": v(31.75, 10.8) * mm, "end": v(31.75, 13.97) * mm});
            skLineSegment(sketch, "E2.4.14.0", {"start": v(31.75, 7.62) * mm, "end": v(34.92, 7.62) * mm});
            skLineSegment(sketch, "E2.4.14.1", {"start": v(34.92, 4.45) * mm, "end": v(34.92, 7.62) * mm});
            skLineSegment(sketch, "E2.4.14.2", {"start": v(31.75, 4.45) * mm, "end": v(34.92, 4.45) * mm});
            skLineSegment(sketch, "E2.4.14.3", {"start": v(31.75, 4.45) * mm, "end": v(31.75, 7.62) * mm});
            skLineSegment(sketch, "E2.5.0.0", {"start": v(38.1, 96.52) * mm, "end": v(41.27, 96.52) * mm});
            skLineSegment(sketch, "E2.5.0.1", {"start": v(41.27, 93.35) * mm, "end": v(41.27, 96.52) * mm});
            skLineSegment(sketch, "E2.5.0.2", {"start": v(38.1, 93.35) * mm, "end": v(41.27, 93.35) * mm});
            skLineSegment(sketch, "E2.5.0.3", {"start": v(38.1, 93.35) * mm, "end": v(38.1, 96.52) * mm});
            skLineSegment(sketch, "E2.5.1.0", {"start": v(38.1, 90.17) * mm, "end": v(41.27, 90.17) * mm});
            skLineSegment(sketch, "E2.5.1.1", {"start": v(41.27, 87) * mm, "end": v(41.27, 90.17) * mm});
            skLineSegment(sketch, "E2.5.1.2", {"start": v(38.1, 87) * mm, "end": v(41.27, 87) * mm});
            skLineSegment(sketch, "E2.5.1.3", {"start": v(38.1, 87) * mm, "end": v(38.1, 90.17) * mm});
            skLineSegment(sketch, "E2.5.2.0", {"start": v(38.1, 83.82) * mm, "end": v(41.27, 83.82) * mm});
            skLineSegment(sketch, "E2.5.2.1", {"start": v(41.27, 80.65) * mm, "end": v(41.27, 83.82) * mm});
            skLineSegment(sketch, "E2.5.2.2", {"start": v(38.1, 80.65) * mm, "end": v(41.27, 80.65) * mm});
            skLineSegment(sketch, "E2.5.2.3", {"start": v(38.1, 80.65) * mm, "end": v(38.1, 83.82) * mm});
            skLineSegment(sketch, "E2.5.3.0", {"start": v(38.1, 77.47) * mm, "end": v(41.27, 77.47) * mm});
            skLineSegment(sketch, "E2.5.3.1", {"start": v(41.27, 74.3) * mm, "end": v(41.27, 77.47) * mm});
            skLineSegment(sketch, "E2.5.3.2", {"start": v(38.1, 74.3) * mm, "end": v(41.27, 74.3) * mm});
            skLineSegment(sketch, "E2.5.3.3", {"start": v(38.1, 74.3) * mm, "end": v(38.1, 77.47) * mm});
            skLineSegment(sketch, "E2.5.4.0", {"start": v(38.1, 71.12) * mm, "end": v(41.27, 71.12) * mm});
            skLineSegment(sketch, "E2.5.4.1", {"start": v(41.27, 67.95) * mm, "end": v(41.27, 71.12) * mm});
            skLineSegment(sketch, "E2.5.4.2", {"start": v(38.1, 67.95) * mm, "end": v(41.27, 67.95) * mm});
            skLineSegment(sketch, "E2.5.4.3", {"start": v(38.1, 67.95) * mm, "end": v(38.1, 71.12) * mm});
            skLineSegment(sketch, "E2.5.5.0", {"start": v(38.1, 64.77) * mm, "end": v(41.27, 64.77) * mm});
            skLineSegment(sketch, "E2.5.5.1", {"start": v(41.27, 61.6) * mm, "end": v(41.27, 64.77) * mm});
            skLineSegment(sketch, "E2.5.5.2", {"start": v(38.1, 61.6) * mm, "end": v(41.27, 61.6) * mm});
            skLineSegment(sketch, "E2.5.5.3", {"start": v(38.1, 61.6) * mm, "end": v(38.1, 64.77) * mm});
            skLineSegment(sketch, "E2.5.6.0", {"start": v(38.1, 58.42) * mm, "end": v(41.27, 58.42) * mm});
            skLineSegment(sketch, "E2.5.6.1", {"start": v(41.27, 55.25) * mm, "end": v(41.27, 58.42) * mm});
            skLineSegment(sketch, "E2.5.6.2", {"start": v(38.1, 55.25) * mm, "end": v(41.27, 55.25) * mm});
            skLineSegment(sketch, "E2.5.6.3", {"start": v(38.1, 55.25) * mm, "end": v(38.1, 58.42) * mm});
            skLineSegment(sketch, "E2.5.7.0", {"start": v(38.1, 52.07) * mm, "end": v(41.27, 52.07) * mm});
            skLineSegment(sketch, "E2.5.7.1", {"start": v(41.27, 48.9) * mm, "end": v(41.27, 52.07) * mm});
            skLineSegment(sketch, "E2.5.7.2", {"start": v(38.1, 48.9) * mm, "end": v(41.27, 48.9) * mm});
            skLineSegment(sketch, "E2.5.7.3", {"start": v(38.1, 48.9) * mm, "end": v(38.1, 52.07) * mm});
            skLineSegment(sketch, "E2.5.8.0", {"start": v(38.1, 45.72) * mm, "end": v(41.27, 45.72) * mm});
            skLineSegment(sketch, "E2.5.8.1", {"start": v(41.27, 42.55) * mm, "end": v(41.27, 45.72) * mm});
            skLineSegment(sketch, "E2.5.8.2", {"start": v(38.1, 42.55) * mm, "end": v(41.27, 42.55) * mm});
            skLineSegment(sketch, "E2.5.8.3", {"start": v(38.1, 42.55) * mm, "end": v(38.1, 45.72) * mm});
            skLineSegment(sketch, "E2.5.9.0", {"start": v(38.1, 39.37) * mm, "end": v(41.27, 39.37) * mm});
            skLineSegment(sketch, "E2.5.9.1", {"start": v(41.27, 36.2) * mm, "end": v(41.27, 39.37) * mm});
            skLineSegment(sketch, "E2.5.9.2", {"start": v(38.1, 36.2) * mm, "end": v(41.27, 36.2) * mm});
            skLineSegment(sketch, "E2.5.9.3", {"start": v(38.1, 36.2) * mm, "end": v(38.1, 39.37) * mm});
            skLineSegment(sketch, "E2.5.10.0", {"start": v(38.1, 33.02) * mm, "end": v(41.27, 33.02) * mm});
            skLineSegment(sketch, "E2.5.10.1", {"start": v(41.27, 29.85) * mm, "end": v(41.27, 33.02) * mm});
            skLineSegment(sketch, "E2.5.10.2", {"start": v(38.1, 29.85) * mm, "end": v(41.27, 29.85) * mm});
            skLineSegment(sketch, "E2.5.10.3", {"start": v(38.1, 29.85) * mm, "end": v(38.1, 33.02) * mm});
            skLineSegment(sketch, "E2.5.11.0", {"start": v(38.1, 26.67) * mm, "end": v(41.27, 26.67) * mm});
            skLineSegment(sketch, "E2.5.11.1", {"start": v(41.27, 23.5) * mm, "end": v(41.27, 26.67) * mm});
            skLineSegment(sketch, "E2.5.11.2", {"start": v(38.1, 23.5) * mm, "end": v(41.27, 23.5) * mm});
            skLineSegment(sketch, "E2.5.11.3", {"start": v(38.1, 23.5) * mm, "end": v(38.1, 26.67) * mm});
            skLineSegment(sketch, "E2.5.12.0", {"start": v(38.1, 20.32) * mm, "end": v(41.27, 20.32) * mm});
            skLineSegment(sketch, "E2.5.12.1", {"start": v(41.27, 17.15) * mm, "end": v(41.27, 20.32) * mm});
            skLineSegment(sketch, "E2.5.12.2", {"start": v(38.1, 17.15) * mm, "end": v(41.27, 17.15) * mm});
            skLineSegment(sketch, "E2.5.12.3", {"start": v(38.1, 17.15) * mm, "end": v(38.1, 20.32) * mm});
            skLineSegment(sketch, "E2.5.13.0", {"start": v(38.1, 13.97) * mm, "end": v(41.27, 13.97) * mm});
            skLineSegment(sketch, "E2.5.13.1", {"start": v(41.27, 10.8) * mm, "end": v(41.27, 13.97) * mm});
            skLineSegment(sketch, "E2.5.13.2", {"start": v(38.1, 10.8) * mm, "end": v(41.27, 10.8) * mm});
            skLineSegment(sketch, "E2.5.13.3", {"start": v(38.1, 10.8) * mm, "end": v(38.1, 13.97) * mm});
            skLineSegment(sketch, "E2.5.14.0", {"start": v(38.1, 7.62) * mm, "end": v(41.27, 7.62) * mm});
            skLineSegment(sketch, "E2.5.14.1", {"start": v(41.27, 4.45) * mm, "end": v(41.27, 7.62) * mm});
            skLineSegment(sketch, "E2.5.14.2", {"start": v(38.1, 4.45) * mm, "end": v(41.27, 4.45) * mm});
            skLineSegment(sketch, "E2.5.14.3", {"start": v(38.1, 4.45) * mm, "end": v(38.1, 7.62) * mm});
            skLineSegment(sketch, "E2.6.0.0", {"start": v(44.45, 96.52) * mm, "end": v(47.62, 96.52) * mm});
            skLineSegment(sketch, "E2.6.0.1", {"start": v(47.62, 93.35) * mm, "end": v(47.62, 96.52) * mm});
            skLineSegment(sketch, "E2.6.0.2", {"start": v(44.45, 93.35) * mm, "end": v(47.62, 93.35) * mm});
            skLineSegment(sketch, "E2.6.0.3", {"start": v(44.45, 93.35) * mm, "end": v(44.45, 96.52) * mm});
            skLineSegment(sketch, "E2.6.1.0", {"start": v(44.45, 90.17) * mm, "end": v(47.62, 90.17) * mm});
            skLineSegment(sketch, "E2.6.1.1", {"start": v(47.62, 87) * mm, "end": v(47.62, 90.17) * mm});
            skLineSegment(sketch, "E2.6.1.2", {"start": v(44.45, 87) * mm, "end": v(47.62, 87) * mm});
            skLineSegment(sketch, "E2.6.1.3", {"start": v(44.45, 87) * mm, "end": v(44.45, 90.17) * mm});
            skLineSegment(sketch, "E2.6.2.0", {"start": v(44.45, 83.82) * mm, "end": v(47.62, 83.82) * mm});
            skLineSegment(sketch, "E2.6.2.1", {"start": v(47.62, 80.65) * mm, "end": v(47.62, 83.82) * mm});
            skLineSegment(sketch, "E2.6.2.2", {"start": v(44.45, 80.65) * mm, "end": v(47.62, 80.65) * mm});
            skLineSegment(sketch, "E2.6.2.3", {"start": v(44.45, 80.65) * mm, "end": v(44.45, 83.82) * mm});
            skLineSegment(sketch, "E2.6.3.0", {"start": v(44.45, 77.47) * mm, "end": v(47.62, 77.47) * mm});
            skLineSegment(sketch, "E2.6.3.1", {"start": v(47.62, 74.3) * mm, "end": v(47.62, 77.47) * mm});
            skLineSegment(sketch, "E2.6.3.2", {"start": v(44.45, 74.3) * mm, "end": v(47.62, 74.3) * mm});
            skLineSegment(sketch, "E2.6.3.3", {"start": v(44.45, 74.3) * mm, "end": v(44.45, 77.47) * mm});
            skLineSegment(sketch, "E2.6.4.0", {"start": v(44.45, 71.12) * mm, "end": v(47.62, 71.12) * mm});
            skLineSegment(sketch, "E2.6.4.1", {"start": v(47.62, 67.95) * mm, "end": v(47.62, 71.12) * mm});
            skLineSegment(sketch, "E2.6.4.2", {"start": v(44.45, 67.95) * mm, "end": v(47.62, 67.95) * mm});
            skLineSegment(sketch, "E2.6.4.3", {"start": v(44.45, 67.95) * mm, "end": v(44.45, 71.12) * mm});
            skLineSegment(sketch, "E2.6.5.0", {"start": v(44.45, 64.77) * mm, "end": v(47.62, 64.77) * mm});
            skLineSegment(sketch, "E2.6.5.1", {"start": v(47.62, 61.6) * mm, "end": v(47.62, 64.77) * mm});
            skLineSegment(sketch, "E2.6.5.2", {"start": v(44.45, 61.6) * mm, "end": v(47.62, 61.6) * mm});
            skLineSegment(sketch, "E2.6.5.3", {"start": v(44.45, 61.6) * mm, "end": v(44.45, 64.77) * mm});
            skLineSegment(sketch, "E2.6.6.0", {"start": v(44.45, 58.42) * mm, "end": v(47.62, 58.42) * mm});
            skLineSegment(sketch, "E2.6.6.1", {"start": v(47.62, 55.25) * mm, "end": v(47.62, 58.42) * mm});
            skLineSegment(sketch, "E2.6.6.2", {"start": v(44.45, 55.25) * mm, "end": v(47.62, 55.25) * mm});
            skLineSegment(sketch, "E2.6.6.3", {"start": v(44.45, 55.25) * mm, "end": v(44.45, 58.42) * mm});
            skLineSegment(sketch, "E2.6.7.0", {"start": v(44.45, 52.07) * mm, "end": v(47.62, 52.07) * mm});
            skLineSegment(sketch, "E2.6.7.1", {"start": v(47.62, 48.9) * mm, "end": v(47.62, 52.07) * mm});
            skLineSegment(sketch, "E2.6.7.2", {"start": v(44.45, 48.9) * mm, "end": v(47.62, 48.9) * mm});
            skLineSegment(sketch, "E2.6.7.3", {"start": v(44.45, 48.9) * mm, "end": v(44.45, 52.07) * mm});
            skLineSegment(sketch, "E2.6.8.0", {"start": v(44.45, 45.72) * mm, "end": v(47.62, 45.72) * mm});
            skLineSegment(sketch, "E2.6.8.1", {"start": v(47.62, 42.55) * mm, "end": v(47.62, 45.72) * mm});
            skLineSegment(sketch, "E2.6.8.2", {"start": v(44.45, 42.55) * mm, "end": v(47.62, 42.55) * mm});
            skLineSegment(sketch, "E2.6.8.3", {"start": v(44.45, 42.55) * mm, "end": v(44.45, 45.72) * mm});
            skLineSegment(sketch, "E2.6.9.0", {"start": v(44.45, 39.37) * mm, "end": v(47.62, 39.37) * mm});
            skLineSegment(sketch, "E2.6.9.1", {"start": v(47.62, 36.2) * mm, "end": v(47.62, 39.37) * mm});
            skLineSegment(sketch, "E2.6.9.2", {"start": v(44.45, 36.2) * mm, "end": v(47.62, 36.2) * mm});
            skLineSegment(sketch, "E2.6.9.3", {"start": v(44.45, 36.2) * mm, "end": v(44.45, 39.37) * mm});
            skLineSegment(sketch, "E2.6.10.0", {"start": v(44.45, 33.02) * mm, "end": v(47.62, 33.02) * mm});
            skLineSegment(sketch, "E2.6.10.1", {"start": v(47.62, 29.85) * mm, "end": v(47.62, 33.02) * mm});
            skLineSegment(sketch, "E2.6.10.2", {"start": v(44.45, 29.85) * mm, "end": v(47.62, 29.85) * mm});
            skLineSegment(sketch, "E2.6.10.3", {"start": v(44.45, 29.85) * mm, "end": v(44.45, 33.02) * mm});
            skLineSegment(sketch, "E2.6.11.0", {"start": v(44.45, 26.67) * mm, "end": v(47.62, 26.67) * mm});
            skLineSegment(sketch, "E2.6.11.1", {"start": v(47.62, 23.5) * mm, "end": v(47.62, 26.67) * mm});
            skLineSegment(sketch, "E2.6.11.2", {"start": v(44.45, 23.5) * mm, "end": v(47.62, 23.5) * mm});
            skLineSegment(sketch, "E2.6.11.3", {"start": v(44.45, 23.5) * mm, "end": v(44.45, 26.67) * mm});
            skLineSegment(sketch, "E2.6.12.0", {"start": v(44.45, 20.32) * mm, "end": v(47.62, 20.32) * mm});
            skLineSegment(sketch, "E2.6.12.1", {"start": v(47.62, 17.15) * mm, "end": v(47.62, 20.32) * mm});
            skLineSegment(sketch, "E2.6.12.2", {"start": v(44.45, 17.15) * mm, "end": v(47.62, 17.15) * mm});
            skLineSegment(sketch, "E2.6.12.3", {"start": v(44.45, 17.15) * mm, "end": v(44.45, 20.32) * mm});
            skLineSegment(sketch, "E2.6.13.0", {"start": v(44.45, 13.97) * mm, "end": v(47.62, 13.97) * mm});
            skLineSegment(sketch, "E2.6.13.1", {"start": v(47.62, 10.8) * mm, "end": v(47.62, 13.97) * mm});
            skLineSegment(sketch, "E2.6.13.2", {"start": v(44.45, 10.8) * mm, "end": v(47.62, 10.8) * mm});
            skLineSegment(sketch, "E2.6.13.3", {"start": v(44.45, 10.8) * mm, "end": v(44.45, 13.97) * mm});
            skLineSegment(sketch, "E2.6.14.0", {"start": v(44.45, 7.62) * mm, "end": v(47.62, 7.62) * mm});
            skLineSegment(sketch, "E2.6.14.1", {"start": v(47.62, 4.45) * mm, "end": v(47.62, 7.62) * mm});
            skLineSegment(sketch, "E2.6.14.2", {"start": v(44.45, 4.45) * mm, "end": v(47.62, 4.45) * mm});
            skLineSegment(sketch, "E2.6.14.3", {"start": v(44.45, 4.45) * mm, "end": v(44.45, 7.62) * mm});
            skLineSegment(sketch, "E2.7.0.0", {"start": v(50.8, 96.52) * mm, "end": v(53.97, 96.52) * mm});
            skLineSegment(sketch, "E2.7.0.1", {"start": v(53.97, 93.35) * mm, "end": v(53.97, 96.52) * mm});
            skLineSegment(sketch, "E2.7.0.2", {"start": v(50.8, 93.35) * mm, "end": v(53.97, 93.35) * mm});
            skLineSegment(sketch, "E2.7.0.3", {"start": v(50.8, 93.35) * mm, "end": v(50.8, 96.52) * mm});
            skLineSegment(sketch, "E2.7.1.0", {"start": v(50.8, 90.17) * mm, "end": v(53.97, 90.17) * mm});
            skLineSegment(sketch, "E2.7.1.1", {"start": v(53.97, 87) * mm, "end": v(53.97, 90.17) * mm});
            skLineSegment(sketch, "E2.7.1.2", {"start": v(50.8, 87) * mm, "end": v(53.97, 87) * mm});
            skLineSegment(sketch, "E2.7.1.3", {"start": v(50.8, 87) * mm, "end": v(50.8, 90.17) * mm});
            skLineSegment(sketch, "E2.7.2.0", {"start": v(50.8, 83.82) * mm, "end": v(53.97, 83.82) * mm});
            skLineSegment(sketch, "E2.7.2.1", {"start": v(53.97, 80.65) * mm, "end": v(53.97, 83.82) * mm});
            skLineSegment(sketch, "E2.7.2.2", {"start": v(50.8, 80.65) * mm, "end": v(53.97, 80.65) * mm});
            skLineSegment(sketch, "E2.7.2.3", {"start": v(50.8, 80.65) * mm, "end": v(50.8, 83.82) * mm});
            skLineSegment(sketch, "E2.7.3.0", {"start": v(50.8, 77.47) * mm, "end": v(53.97, 77.47) * mm});
            skLineSegment(sketch, "E2.7.3.1", {"start": v(53.97, 74.3) * mm, "end": v(53.97, 77.47) * mm});
            skLineSegment(sketch, "E2.7.3.2", {"start": v(50.8, 74.3) * mm, "end": v(53.97, 74.3) * mm});
            skLineSegment(sketch, "E2.7.3.3", {"start": v(50.8, 74.3) * mm, "end": v(50.8, 77.47) * mm});
            skLineSegment(sketch, "E2.7.4.0", {"start": v(50.8, 71.12) * mm, "end": v(53.97, 71.12) * mm});
            skLineSegment(sketch, "E2.7.4.1", {"start": v(53.97, 67.95) * mm, "end": v(53.97, 71.12) * mm});
            skLineSegment(sketch, "E2.7.4.2", {"start": v(50.8, 67.95) * mm, "end": v(53.97, 67.95) * mm});
            skLineSegment(sketch, "E2.7.4.3", {"start": v(50.8, 67.95) * mm, "end": v(50.8, 71.12) * mm});
            skLineSegment(sketch, "E2.7.5.0", {"start": v(50.8, 64.77) * mm, "end": v(53.97, 64.77) * mm});
            skLineSegment(sketch, "E2.7.5.1", {"start": v(53.97, 61.6) * mm, "end": v(53.97, 64.77) * mm});
            skLineSegment(sketch, "E2.7.5.2", {"start": v(50.8, 61.6) * mm, "end": v(53.97, 61.6) * mm});
            skLineSegment(sketch, "E2.7.5.3", {"start": v(50.8, 61.6) * mm, "end": v(50.8, 64.77) * mm});
            skLineSegment(sketch, "E2.7.6.0", {"start": v(50.8, 58.42) * mm, "end": v(53.97, 58.42) * mm});
            skLineSegment(sketch, "E2.7.6.1", {"start": v(53.97, 55.25) * mm, "end": v(53.97, 58.42) * mm});
            skLineSegment(sketch, "E2.7.6.2", {"start": v(50.8, 55.25) * mm, "end": v(53.97, 55.25) * mm});
            skLineSegment(sketch, "E2.7.6.3", {"start": v(50.8, 55.25) * mm, "end": v(50.8, 58.42) * mm});
            skLineSegment(sketch, "E2.7.7.0", {"start": v(50.8, 52.07) * mm, "end": v(53.97, 52.07) * mm});
            skLineSegment(sketch, "E2.7.7.1", {"start": v(53.97, 48.9) * mm, "end": v(53.97, 52.07) * mm});
            skLineSegment(sketch, "E2.7.7.2", {"start": v(50.8, 48.9) * mm, "end": v(53.97, 48.9) * mm});
            skLineSegment(sketch, "E2.7.7.3", {"start": v(50.8, 48.9) * mm, "end": v(50.8, 52.07) * mm});
            skLineSegment(sketch, "E2.7.8.0", {"start": v(50.8, 45.72) * mm, "end": v(53.97, 45.72) * mm});
            skLineSegment(sketch, "E2.7.8.1", {"start": v(53.97, 42.55) * mm, "end": v(53.97, 45.72) * mm});
            skLineSegment(sketch, "E2.7.8.2", {"start": v(50.8, 42.55) * mm, "end": v(53.97, 42.55) * mm});
            skLineSegment(sketch, "E2.7.8.3", {"start": v(50.8, 42.55) * mm, "end": v(50.8, 45.72) * mm});
            skLineSegment(sketch, "E2.7.9.0", {"start": v(50.8, 39.37) * mm, "end": v(53.97, 39.37) * mm});
            skLineSegment(sketch, "E2.7.9.1", {"start": v(53.97, 36.2) * mm, "end": v(53.97, 39.37) * mm});
            skLineSegment(sketch, "E2.7.9.2", {"start": v(50.8, 36.2) * mm, "end": v(53.97, 36.2) * mm});
            skLineSegment(sketch, "E2.7.9.3", {"start": v(50.8, 36.2) * mm, "end": v(50.8, 39.37) * mm});
            skLineSegment(sketch, "E2.7.10.0", {"start": v(50.8, 33.02) * mm, "end": v(53.97, 33.02) * mm});
            skLineSegment(sketch, "E2.7.10.1", {"start": v(53.97, 29.85) * mm, "end": v(53.97, 33.02) * mm});
            skLineSegment(sketch, "E2.7.10.2", {"start": v(50.8, 29.85) * mm, "end": v(53.97, 29.85) * mm});
            skLineSegment(sketch, "E2.7.10.3", {"start": v(50.8, 29.85) * mm, "end": v(50.8, 33.02) * mm});
            skLineSegment(sketch, "E2.7.11.0", {"start": v(50.8, 26.67) * mm, "end": v(53.97, 26.67) * mm});
            skLineSegment(sketch, "E2.7.11.1", {"start": v(53.97, 23.5) * mm, "end": v(53.97, 26.67) * mm});
            skLineSegment(sketch, "E2.7.11.2", {"start": v(50.8, 23.5) * mm, "end": v(53.97, 23.5) * mm});
            skLineSegment(sketch, "E2.7.11.3", {"start": v(50.8, 23.5) * mm, "end": v(50.8, 26.67) * mm});
            skLineSegment(sketch, "E2.7.12.0", {"start": v(50.8, 20.32) * mm, "end": v(53.97, 20.32) * mm});
            skLineSegment(sketch, "E2.7.12.1", {"start": v(53.97, 17.15) * mm, "end": v(53.97, 20.32) * mm});
            skLineSegment(sketch, "E2.7.12.2", {"start": v(50.8, 17.15) * mm, "end": v(53.97, 17.15) * mm});
            skLineSegment(sketch, "E2.7.12.3", {"start": v(50.8, 17.15) * mm, "end": v(50.8, 20.32) * mm});
            skLineSegment(sketch, "E2.7.13.0", {"start": v(50.8, 13.97) * mm, "end": v(53.97, 13.97) * mm});
            skLineSegment(sketch, "E2.7.13.1", {"start": v(53.97, 10.8) * mm, "end": v(53.97, 13.97) * mm});
            skLineSegment(sketch, "E2.7.13.2", {"start": v(50.8, 10.8) * mm, "end": v(53.97, 10.8) * mm});
            skLineSegment(sketch, "E2.7.13.3", {"start": v(50.8, 10.8) * mm, "end": v(50.8, 13.97) * mm});
            skLineSegment(sketch, "E2.7.14.0", {"start": v(50.8, 7.62) * mm, "end": v(53.97, 7.62) * mm});
            skLineSegment(sketch, "E2.7.14.1", {"start": v(53.97, 4.45) * mm, "end": v(53.97, 7.62) * mm});
            skLineSegment(sketch, "E2.7.14.2", {"start": v(50.8, 4.45) * mm, "end": v(53.97, 4.45) * mm});
            skLineSegment(sketch, "E2.7.14.3", {"start": v(50.8, 4.45) * mm, "end": v(50.8, 7.62) * mm});
            skLineSegment(sketch, "E2.8.0.0", {"start": v(57.15, 96.52) * mm, "end": v(60.32, 96.52) * mm});
            skLineSegment(sketch, "E2.8.0.1", {"start": v(60.32, 93.35) * mm, "end": v(60.32, 96.52) * mm});
            skLineSegment(sketch, "E2.8.0.2", {"start": v(57.15, 93.35) * mm, "end": v(60.32, 93.35) * mm});
            skLineSegment(sketch, "E2.8.0.3", {"start": v(57.15, 93.35) * mm, "end": v(57.15, 96.52) * mm});
            skLineSegment(sketch, "E2.8.1.0", {"start": v(57.15, 90.17) * mm, "end": v(60.32, 90.17) * mm});
            skLineSegment(sketch, "E2.8.1.1", {"start": v(60.32, 87) * mm, "end": v(60.32, 90.17) * mm});
            skLineSegment(sketch, "E2.8.1.2", {"start": v(57.15, 87) * mm, "end": v(60.32, 87) * mm});
            skLineSegment(sketch, "E2.8.1.3", {"start": v(57.15, 87) * mm, "end": v(57.15, 90.17) * mm});
            skLineSegment(sketch, "E2.8.2.0", {"start": v(57.15, 83.82) * mm, "end": v(60.32, 83.82) * mm});
            skLineSegment(sketch, "E2.8.2.1", {"start": v(60.32, 80.65) * mm, "end": v(60.32, 83.82) * mm});
            skLineSegment(sketch, "E2.8.2.2", {"start": v(57.15, 80.65) * mm, "end": v(60.32, 80.65) * mm});
            skLineSegment(sketch, "E2.8.2.3", {"start": v(57.15, 80.65) * mm, "end": v(57.15, 83.82) * mm});
            skLineSegment(sketch, "E2.8.3.0", {"start": v(57.15, 77.47) * mm, "end": v(60.32, 77.47) * mm});
            skLineSegment(sketch, "E2.8.3.1", {"start": v(60.32, 74.3) * mm, "end": v(60.32, 77.47) * mm});
            skLineSegment(sketch, "E2.8.3.2", {"start": v(57.15, 74.3) * mm, "end": v(60.32, 74.3) * mm});
            skLineSegment(sketch, "E2.8.3.3", {"start": v(57.15, 74.3) * mm, "end": v(57.15, 77.47) * mm});
            skLineSegment(sketch, "E2.8.4.0", {"start": v(57.15, 71.12) * mm, "end": v(60.32, 71.12) * mm});
            skLineSegment(sketch, "E2.8.4.1", {"start": v(60.32, 67.95) * mm, "end": v(60.32, 71.12) * mm});
            skLineSegment(sketch, "E2.8.4.2", {"start": v(57.15, 67.95) * mm, "end": v(60.32, 67.95) * mm});
            skLineSegment(sketch, "E2.8.4.3", {"start": v(57.15, 67.95) * mm, "end": v(57.15, 71.12) * mm});
            skLineSegment(sketch, "E2.8.5.0", {"start": v(57.15, 64.77) * mm, "end": v(60.32, 64.77) * mm});
            skLineSegment(sketch, "E2.8.5.1", {"start": v(60.32, 61.6) * mm, "end": v(60.32, 64.77) * mm});
            skLineSegment(sketch, "E2.8.5.2", {"start": v(57.15, 61.6) * mm, "end": v(60.32, 61.6) * mm});
            skLineSegment(sketch, "E2.8.5.3", {"start": v(57.15, 61.6) * mm, "end": v(57.15, 64.77) * mm});
            skLineSegment(sketch, "E2.8.6.0", {"start": v(57.15, 58.42) * mm, "end": v(60.32, 58.42) * mm});
            skLineSegment(sketch, "E2.8.6.1", {"start": v(60.32, 55.25) * mm, "end": v(60.32, 58.42) * mm});
            skLineSegment(sketch, "E2.8.6.2", {"start": v(57.15, 55.25) * mm, "end": v(60.32, 55.25) * mm});
            skLineSegment(sketch, "E2.8.6.3", {"start": v(57.15, 55.25) * mm, "end": v(57.15, 58.42) * mm});
            skLineSegment(sketch, "E2.8.7.0", {"start": v(57.15, 52.07) * mm, "end": v(60.32, 52.07) * mm});
            skLineSegment(sketch, "E2.8.7.1", {"start": v(60.32, 48.9) * mm, "end": v(60.32, 52.07) * mm});
            skLineSegment(sketch, "E2.8.7.2", {"start": v(57.15, 48.9) * mm, "end": v(60.32, 48.9) * mm});
            skLineSegment(sketch, "E2.8.7.3", {"start": v(57.15, 48.9) * mm, "end": v(57.15, 52.07) * mm});
            skLineSegment(sketch, "E2.8.8.0", {"start": v(57.15, 45.72) * mm, "end": v(60.32, 45.72) * mm});
            skLineSegment(sketch, "E2.8.8.1", {"start": v(60.32, 42.55) * mm, "end": v(60.32, 45.72) * mm});
            skLineSegment(sketch, "E2.8.8.2", {"start": v(57.15, 42.55) * mm, "end": v(60.32, 42.55) * mm});
            skLineSegment(sketch, "E2.8.8.3", {"start": v(57.15, 42.55) * mm, "end": v(57.15, 45.72) * mm});
            skLineSegment(sketch, "E2.8.9.0", {"start": v(57.15, 39.37) * mm, "end": v(60.32, 39.37) * mm});
            skLineSegment(sketch, "E2.8.9.1", {"start": v(60.32, 36.2) * mm, "end": v(60.32, 39.37) * mm});
            skLineSegment(sketch, "E2.8.9.2", {"start": v(57.15, 36.2) * mm, "end": v(60.32, 36.2) * mm});
            skLineSegment(sketch, "E2.8.9.3", {"start": v(57.15, 36.2) * mm, "end": v(57.15, 39.37) * mm});
            skLineSegment(sketch, "E2.8.10.0", {"start": v(57.15, 33.02) * mm, "end": v(60.32, 33.02) * mm});
            skLineSegment(sketch, "E2.8.10.1", {"start": v(60.32, 29.85) * mm, "end": v(60.32, 33.02) * mm});
            skLineSegment(sketch, "E2.8.10.2", {"start": v(57.15, 29.85) * mm, "end": v(60.32, 29.85) * mm});
            skLineSegment(sketch, "E2.8.10.3", {"start": v(57.15, 29.85) * mm, "end": v(57.15, 33.02) * mm});
            skLineSegment(sketch, "E2.8.11.0", {"start": v(57.15, 26.67) * mm, "end": v(60.32, 26.67) * mm});
            skLineSegment(sketch, "E2.8.11.1", {"start": v(60.32, 23.5) * mm, "end": v(60.32, 26.67) * mm});
            skLineSegment(sketch, "E2.8.11.2", {"start": v(57.15, 23.5) * mm, "end": v(60.32, 23.5) * mm});
            skLineSegment(sketch, "E2.8.11.3", {"start": v(57.15, 23.5) * mm, "end": v(57.15, 26.67) * mm});
            skLineSegment(sketch, "E2.8.12.0", {"start": v(57.15, 20.32) * mm, "end": v(60.32, 20.32) * mm});
            skLineSegment(sketch, "E2.8.12.1", {"start": v(60.32, 17.15) * mm, "end": v(60.32, 20.32) * mm});
            skLineSegment(sketch, "E2.8.12.2", {"start": v(57.15, 17.15) * mm, "end": v(60.32, 17.15) * mm});
            skLineSegment(sketch, "E2.8.12.3", {"start": v(57.15, 17.15) * mm, "end": v(57.15, 20.32) * mm});
            skLineSegment(sketch, "E2.8.13.0", {"start": v(57.15, 13.97) * mm, "end": v(60.32, 13.97) * mm});
            skLineSegment(sketch, "E2.8.13.1", {"start": v(60.32, 10.8) * mm, "end": v(60.32, 13.97) * mm});
            skLineSegment(sketch, "E2.8.13.2", {"start": v(57.15, 10.8) * mm, "end": v(60.32, 10.8) * mm});
            skLineSegment(sketch, "E2.8.13.3", {"start": v(57.15, 10.8) * mm, "end": v(57.15, 13.97) * mm});
            skLineSegment(sketch, "E2.8.14.0", {"start": v(57.15, 7.62) * mm, "end": v(60.32, 7.62) * mm});
            skLineSegment(sketch, "E2.8.14.1", {"start": v(60.32, 4.45) * mm, "end": v(60.32, 7.62) * mm});
            skLineSegment(sketch, "E2.8.14.2", {"start": v(57.15, 4.45) * mm, "end": v(60.32, 4.45) * mm});
            skLineSegment(sketch, "E2.8.14.3", {"start": v(57.15, 4.45) * mm, "end": v(57.15, 7.62) * mm});
            skLineSegment(sketch, "E2.9.0.0", {"start": v(63.5, 96.52) * mm, "end": v(66.67, 96.52) * mm});
            skLineSegment(sketch, "E2.9.0.1", {"start": v(66.67, 93.35) * mm, "end": v(66.67, 96.52) * mm});
            skLineSegment(sketch, "E2.9.0.2", {"start": v(63.5, 93.35) * mm, "end": v(66.67, 93.35) * mm});
            skLineSegment(sketch, "E2.9.0.3", {"start": v(63.5, 93.35) * mm, "end": v(63.5, 96.52) * mm});
            skLineSegment(sketch, "E2.9.1.0", {"start": v(63.5, 90.17) * mm, "end": v(66.67, 90.17) * mm});
            skLineSegment(sketch, "E2.9.1.1", {"start": v(66.67, 87) * mm, "end": v(66.67, 90.17) * mm});
            skLineSegment(sketch, "E2.9.1.2", {"start": v(63.5, 87) * mm, "end": v(66.67, 87) * mm});
            skLineSegment(sketch, "E2.9.1.3", {"start": v(63.5, 87) * mm, "end": v(63.5, 90.17) * mm});
            skLineSegment(sketch, "E2.9.2.0", {"start": v(63.5, 83.82) * mm, "end": v(66.67, 83.82) * mm});
            skLineSegment(sketch, "E2.9.2.1", {"start": v(66.67, 80.65) * mm, "end": v(66.67, 83.82) * mm});
            skLineSegment(sketch, "E2.9.2.2", {"start": v(63.5, 80.65) * mm, "end": v(66.67, 80.65) * mm});
            skLineSegment(sketch, "E2.9.2.3", {"start": v(63.5, 80.65) * mm, "end": v(63.5, 83.82) * mm});
            skLineSegment(sketch, "E2.9.3.0", {"start": v(63.5, 77.47) * mm, "end": v(66.67, 77.47) * mm});
            skLineSegment(sketch, "E2.9.3.1", {"start": v(66.67, 74.3) * mm, "end": v(66.67, 77.47) * mm});
            skLineSegment(sketch, "E2.9.3.2", {"start": v(63.5, 74.3) * mm, "end": v(66.67, 74.3) * mm});
            skLineSegment(sketch, "E2.9.3.3", {"start": v(63.5, 74.3) * mm, "end": v(63.5, 77.47) * mm});
            skLineSegment(sketch, "E2.9.4.0", {"start": v(63.5, 71.12) * mm, "end": v(66.67, 71.12) * mm});
            skLineSegment(sketch, "E2.9.4.1", {"start": v(66.67, 67.95) * mm, "end": v(66.67, 71.12) * mm});
            skLineSegment(sketch, "E2.9.4.2", {"start": v(63.5, 67.95) * mm, "end": v(66.67, 67.95) * mm});
            skLineSegment(sketch, "E2.9.4.3", {"start": v(63.5, 67.95) * mm, "end": v(63.5, 71.12) * mm});
            skLineSegment(sketch, "E2.9.5.0", {"start": v(63.5, 64.77) * mm, "end": v(66.67, 64.77) * mm});
            skLineSegment(sketch, "E2.9.5.1", {"start": v(66.67, 61.6) * mm, "end": v(66.67, 64.77) * mm});
            skLineSegment(sketch, "E2.9.5.2", {"start": v(63.5, 61.6) * mm, "end": v(66.67, 61.6) * mm});
            skLineSegment(sketch, "E2.9.5.3", {"start": v(63.5, 61.6) * mm, "end": v(63.5, 64.77) * mm});
            skLineSegment(sketch, "E2.9.6.0", {"start": v(63.5, 58.42) * mm, "end": v(66.67, 58.42) * mm});
            skLineSegment(sketch, "E2.9.6.1", {"start": v(66.67, 55.25) * mm, "end": v(66.67, 58.42) * mm});
            skLineSegment(sketch, "E2.9.6.2", {"start": v(63.5, 55.25) * mm, "end": v(66.67, 55.25) * mm});
            skLineSegment(sketch, "E2.9.6.3", {"start": v(63.5, 55.25) * mm, "end": v(63.5, 58.42) * mm});
            skLineSegment(sketch, "E2.9.7.0", {"start": v(63.5, 52.07) * mm, "end": v(66.67, 52.07) * mm});
            skLineSegment(sketch, "E2.9.7.1", {"start": v(66.67, 48.9) * mm, "end": v(66.67, 52.07) * mm});
            skLineSegment(sketch, "E2.9.7.2", {"start": v(63.5, 48.9) * mm, "end": v(66.67, 48.9) * mm});
            skLineSegment(sketch, "E2.9.7.3", {"start": v(63.5, 48.9) * mm, "end": v(63.5, 52.07) * mm});
            skLineSegment(sketch, "E2.9.8.0", {"start": v(63.5, 45.72) * mm, "end": v(66.67, 45.72) * mm});
            skLineSegment(sketch, "E2.9.8.1", {"start": v(66.67, 42.55) * mm, "end": v(66.67, 45.72) * mm});
            skLineSegment(sketch, "E2.9.8.2", {"start": v(63.5, 42.55) * mm, "end": v(66.67, 42.55) * mm});
            skLineSegment(sketch, "E2.9.8.3", {"start": v(63.5, 42.55) * mm, "end": v(63.5, 45.72) * mm});
            skLineSegment(sketch, "E2.9.9.0", {"start": v(63.5, 39.37) * mm, "end": v(66.67, 39.37) * mm});
            skLineSegment(sketch, "E2.9.9.1", {"start": v(66.67, 36.2) * mm, "end": v(66.67, 39.37) * mm});
            skLineSegment(sketch, "E2.9.9.2", {"start": v(63.5, 36.2) * mm, "end": v(66.67, 36.2) * mm});
            skLineSegment(sketch, "E2.9.9.3", {"start": v(63.5, 36.2) * mm, "end": v(63.5, 39.37) * mm});
            skLineSegment(sketch, "E2.9.10.0", {"start": v(63.5, 33.02) * mm, "end": v(66.67, 33.02) * mm});
            skLineSegment(sketch, "E2.9.10.1", {"start": v(66.67, 29.85) * mm, "end": v(66.67, 33.02) * mm});
            skLineSegment(sketch, "E2.9.10.2", {"start": v(63.5, 29.85) * mm, "end": v(66.67, 29.85) * mm});
            skLineSegment(sketch, "E2.9.10.3", {"start": v(63.5, 29.85) * mm, "end": v(63.5, 33.02) * mm});
            skLineSegment(sketch, "E2.9.11.0", {"start": v(63.5, 26.67) * mm, "end": v(66.67, 26.67) * mm});
            skLineSegment(sketch, "E2.9.11.1", {"start": v(66.67, 23.5) * mm, "end": v(66.67, 26.67) * mm});
            skLineSegment(sketch, "E2.9.11.2", {"start": v(63.5, 23.5) * mm, "end": v(66.67, 23.5) * mm});
            skLineSegment(sketch, "E2.9.11.3", {"start": v(63.5, 23.5) * mm, "end": v(63.5, 26.67) * mm});
            skLineSegment(sketch, "E2.9.12.0", {"start": v(63.5, 20.32) * mm, "end": v(66.67, 20.32) * mm});
            skLineSegment(sketch, "E2.9.12.1", {"start": v(66.67, 17.15) * mm, "end": v(66.67, 20.32) * mm});
            skLineSegment(sketch, "E2.9.12.2", {"start": v(63.5, 17.15) * mm, "end": v(66.67, 17.15) * mm});
            skLineSegment(sketch, "E2.9.12.3", {"start": v(63.5, 17.15) * mm, "end": v(63.5, 20.32) * mm});
            skLineSegment(sketch, "E2.9.13.0", {"start": v(63.5, 13.97) * mm, "end": v(66.67, 13.97) * mm});
            skLineSegment(sketch, "E2.9.13.1", {"start": v(66.67, 10.8) * mm, "end": v(66.67, 13.97) * mm});
            skLineSegment(sketch, "E2.9.13.2", {"start": v(63.5, 10.8) * mm, "end": v(66.67, 10.8) * mm});
            skLineSegment(sketch, "E2.9.13.3", {"start": v(63.5, 10.8) * mm, "end": v(63.5, 13.97) * mm});
            skLineSegment(sketch, "E2.9.14.0", {"start": v(63.5, 7.62) * mm, "end": v(66.67, 7.62) * mm});
            skLineSegment(sketch, "E2.9.14.1", {"start": v(66.67, 4.45) * mm, "end": v(66.67, 7.62) * mm});
            skLineSegment(sketch, "E2.9.14.2", {"start": v(63.5, 4.45) * mm, "end": v(66.67, 4.45) * mm});
            skLineSegment(sketch, "E2.9.14.3", {"start": v(63.5, 4.45) * mm, "end": v(63.5, 7.62) * mm});
            skLineSegment(sketch, "E2.10.0.0", {"start": v(69.85, 96.52) * mm, "end": v(73.02, 96.52) * mm});
            skLineSegment(sketch, "E2.10.0.1", {"start": v(73.02, 93.35) * mm, "end": v(73.02, 96.52) * mm});
            skLineSegment(sketch, "E2.10.0.2", {"start": v(69.85, 93.35) * mm, "end": v(73.02, 93.35) * mm});
            skLineSegment(sketch, "E2.10.0.3", {"start": v(69.85, 93.35) * mm, "end": v(69.85, 96.52) * mm});
            skLineSegment(sketch, "E2.10.1.0", {"start": v(69.85, 90.17) * mm, "end": v(73.02, 90.17) * mm});
            skLineSegment(sketch, "E2.10.1.1", {"start": v(73.02, 87) * mm, "end": v(73.02, 90.17) * mm});
            skLineSegment(sketch, "E2.10.1.2", {"start": v(69.85, 87) * mm, "end": v(73.02, 87) * mm});
            skLineSegment(sketch, "E2.10.1.3", {"start": v(69.85, 87) * mm, "end": v(69.85, 90.17) * mm});
            skLineSegment(sketch, "E2.10.2.0", {"start": v(69.85, 83.82) * mm, "end": v(73.02, 83.82) * mm});
            skLineSegment(sketch, "E2.10.2.1", {"start": v(73.02, 80.65) * mm, "end": v(73.02, 83.82) * mm});
            skLineSegment(sketch, "E2.10.2.2", {"start": v(69.85, 80.65) * mm, "end": v(73.02, 80.65) * mm});
            skLineSegment(sketch, "E2.10.2.3", {"start": v(69.85, 80.65) * mm, "end": v(69.85, 83.82) * mm});
            skLineSegment(sketch, "E2.10.3.0", {"start": v(69.85, 77.47) * mm, "end": v(73.02, 77.47) * mm});
            skLineSegment(sketch, "E2.10.3.1", {"start": v(73.02, 74.3) * mm, "end": v(73.02, 77.47) * mm});
            skLineSegment(sketch, "E2.10.3.2", {"start": v(69.85, 74.3) * mm, "end": v(73.02, 74.3) * mm});
            skLineSegment(sketch, "E2.10.3.3", {"start": v(69.85, 74.3) * mm, "end": v(69.85, 77.47) * mm});
            skLineSegment(sketch, "E2.10.4.0", {"start": v(69.85, 71.12) * mm, "end": v(73.02, 71.12) * mm});
            skLineSegment(sketch, "E2.10.4.1", {"start": v(73.02, 67.95) * mm, "end": v(73.02, 71.12) * mm});
            skLineSegment(sketch, "E2.10.4.2", {"start": v(69.85, 67.95) * mm, "end": v(73.02, 67.95) * mm});
            skLineSegment(sketch, "E2.10.4.3", {"start": v(69.85, 67.95) * mm, "end": v(69.85, 71.12) * mm});
            skLineSegment(sketch, "E2.10.5.0", {"start": v(69.85, 64.77) * mm, "end": v(73.02, 64.77) * mm});
            skLineSegment(sketch, "E2.10.5.1", {"start": v(73.02, 61.6) * mm, "end": v(73.02, 64.77) * mm});
            skLineSegment(sketch, "E2.10.5.2", {"start": v(69.85, 61.6) * mm, "end": v(73.02, 61.6) * mm});
            skLineSegment(sketch, "E2.10.5.3", {"start": v(69.85, 61.6) * mm, "end": v(69.85, 64.77) * mm});
            skLineSegment(sketch, "E2.10.6.0", {"start": v(69.85, 58.42) * mm, "end": v(73.02, 58.42) * mm});
            skLineSegment(sketch, "E2.10.6.1", {"start": v(73.02, 55.25) * mm, "end": v(73.02, 58.42) * mm});
            skLineSegment(sketch, "E2.10.6.2", {"start": v(69.85, 55.25) * mm, "end": v(73.02, 55.25) * mm});
            skLineSegment(sketch, "E2.10.6.3", {"start": v(69.85, 55.25) * mm, "end": v(69.85, 58.42) * mm});
            skLineSegment(sketch, "E2.10.7.0", {"start": v(69.85, 52.07) * mm, "end": v(73.02, 52.07) * mm});
            skLineSegment(sketch, "E2.10.7.1", {"start": v(73.02, 48.9) * mm, "end": v(73.02, 52.07) * mm});
            skLineSegment(sketch, "E2.10.7.2", {"start": v(69.85, 48.9) * mm, "end": v(73.02, 48.9) * mm});
            skLineSegment(sketch, "E2.10.7.3", {"start": v(69.85, 48.9) * mm, "end": v(69.85, 52.07) * mm});
            skLineSegment(sketch, "E2.10.8.0", {"start": v(69.85, 45.72) * mm, "end": v(73.02, 45.72) * mm});
            skLineSegment(sketch, "E2.10.8.1", {"start": v(73.02, 42.55) * mm, "end": v(73.02, 45.72) * mm});
            skLineSegment(sketch, "E2.10.8.2", {"start": v(69.85, 42.55) * mm, "end": v(73.02, 42.55) * mm});
            skLineSegment(sketch, "E2.10.8.3", {"start": v(69.85, 42.55) * mm, "end": v(69.85, 45.72) * mm});
            skLineSegment(sketch, "E2.10.9.0", {"start": v(69.85, 39.37) * mm, "end": v(73.02, 39.37) * mm});
            skLineSegment(sketch, "E2.10.9.1", {"start": v(73.02, 36.2) * mm, "end": v(73.02, 39.37) * mm});
            skLineSegment(sketch, "E2.10.9.2", {"start": v(69.85, 36.2) * mm, "end": v(73.02, 36.2) * mm});
            skLineSegment(sketch, "E2.10.9.3", {"start": v(69.85, 36.2) * mm, "end": v(69.85, 39.37) * mm});
            skLineSegment(sketch, "E2.10.10.0", {"start": v(69.85, 33.02) * mm, "end": v(73.02, 33.02) * mm});
            skLineSegment(sketch, "E2.10.10.1", {"start": v(73.02, 29.85) * mm, "end": v(73.02, 33.02) * mm});
            skLineSegment(sketch, "E2.10.10.2", {"start": v(69.85, 29.85) * mm, "end": v(73.02, 29.85) * mm});
            skLineSegment(sketch, "E2.10.10.3", {"start": v(69.85, 29.85) * mm, "end": v(69.85, 33.02) * mm});
            skLineSegment(sketch, "E2.10.11.0", {"start": v(69.85, 26.67) * mm, "end": v(73.02, 26.67) * mm});
            skLineSegment(sketch, "E2.10.11.1", {"start": v(73.02, 23.5) * mm, "end": v(73.02, 26.67) * mm});
            skLineSegment(sketch, "E2.10.11.2", {"start": v(69.85, 23.5) * mm, "end": v(73.02, 23.5) * mm});
            skLineSegment(sketch, "E2.10.11.3", {"start": v(69.85, 23.5) * mm, "end": v(69.85, 26.67) * mm});
            skLineSegment(sketch, "E2.10.12.0", {"start": v(69.85, 20.32) * mm, "end": v(73.02, 20.32) * mm});
            skLineSegment(sketch, "E2.10.12.1", {"start": v(73.02, 17.15) * mm, "end": v(73.02, 20.32) * mm});
            skLineSegment(sketch, "E2.10.12.2", {"start": v(69.85, 17.15) * mm, "end": v(73.02, 17.15) * mm});
            skLineSegment(sketch, "E2.10.12.3", {"start": v(69.85, 17.15) * mm, "end": v(69.85, 20.32) * mm});
            skLineSegment(sketch, "E2.10.13.0", {"start": v(69.85, 13.97) * mm, "end": v(73.02, 13.97) * mm});
            skLineSegment(sketch, "E2.10.13.1", {"start": v(73.02, 10.8) * mm, "end": v(73.02, 13.97) * mm});
            skLineSegment(sketch, "E2.10.13.2", {"start": v(69.85, 10.8) * mm, "end": v(73.02, 10.8) * mm});
            skLineSegment(sketch, "E2.10.13.3", {"start": v(69.85, 10.8) * mm, "end": v(69.85, 13.97) * mm});
            skLineSegment(sketch, "E2.10.14.0", {"start": v(69.85, 7.62) * mm, "end": v(73.02, 7.62) * mm});
            skLineSegment(sketch, "E2.10.14.1", {"start": v(73.02, 4.45) * mm, "end": v(73.02, 7.62) * mm});
            skLineSegment(sketch, "E2.10.14.2", {"start": v(69.85, 4.45) * mm, "end": v(73.02, 4.45) * mm});
            skLineSegment(sketch, "E2.10.14.3", {"start": v(69.85, 4.45) * mm, "end": v(69.85, 7.62) * mm});
            skLineSegment(sketch, "E2.11.0.0", {"start": v(76.2, 96.52) * mm, "end": v(79.37, 96.52) * mm});
            skLineSegment(sketch, "E2.11.0.1", {"start": v(79.37, 93.35) * mm, "end": v(79.37, 96.52) * mm});
            skLineSegment(sketch, "E2.11.0.2", {"start": v(76.2, 93.35) * mm, "end": v(79.37, 93.35) * mm});
            skLineSegment(sketch, "E2.11.0.3", {"start": v(76.2, 93.35) * mm, "end": v(76.2, 96.52) * mm});
            skLineSegment(sketch, "E2.11.1.0", {"start": v(76.2, 90.17) * mm, "end": v(79.37, 90.17) * mm});
            skLineSegment(sketch, "E2.11.1.1", {"start": v(79.37, 87) * mm, "end": v(79.37, 90.17) * mm});
            skLineSegment(sketch, "E2.11.1.2", {"start": v(76.2, 87) * mm, "end": v(79.37, 87) * mm});
            skLineSegment(sketch, "E2.11.1.3", {"start": v(76.2, 87) * mm, "end": v(76.2, 90.17) * mm});
            skLineSegment(sketch, "E2.11.2.0", {"start": v(76.2, 83.82) * mm, "end": v(79.37, 83.82) * mm});
            skLineSegment(sketch, "E2.11.2.1", {"start": v(79.37, 80.65) * mm, "end": v(79.37, 83.82) * mm});
            skLineSegment(sketch, "E2.11.2.2", {"start": v(76.2, 80.65) * mm, "end": v(79.37, 80.65) * mm});
            skLineSegment(sketch, "E2.11.2.3", {"start": v(76.2, 80.65) * mm, "end": v(76.2, 83.82) * mm});
            skLineSegment(sketch, "E2.11.3.0", {"start": v(76.2, 77.47) * mm, "end": v(79.37, 77.47) * mm});
            skLineSegment(sketch, "E2.11.3.1", {"start": v(79.37, 74.3) * mm, "end": v(79.37, 77.47) * mm});
            skLineSegment(sketch, "E2.11.3.2", {"start": v(76.2, 74.3) * mm, "end": v(79.37, 74.3) * mm});
            skLineSegment(sketch, "E2.11.3.3", {"start": v(76.2, 74.3) * mm, "end": v(76.2, 77.47) * mm});
            skLineSegment(sketch, "E2.11.4.0", {"start": v(76.2, 71.12) * mm, "end": v(79.37, 71.12) * mm});
            skLineSegment(sketch, "E2.11.4.1", {"start": v(79.37, 67.95) * mm, "end": v(79.37, 71.12) * mm});
            skLineSegment(sketch, "E2.11.4.2", {"start": v(76.2, 67.95) * mm, "end": v(79.37, 67.95) * mm});
            skLineSegment(sketch, "E2.11.4.3", {"start": v(76.2, 67.95) * mm, "end": v(76.2, 71.12) * mm});
            skLineSegment(sketch, "E2.11.5.0", {"start": v(76.2, 64.77) * mm, "end": v(79.37, 64.77) * mm});
            skLineSegment(sketch, "E2.11.5.1", {"start": v(79.37, 61.6) * mm, "end": v(79.37, 64.77) * mm});
            skLineSegment(sketch, "E2.11.5.2", {"start": v(76.2, 61.6) * mm, "end": v(79.37, 61.6) * mm});
            skLineSegment(sketch, "E2.11.5.3", {"start": v(76.2, 61.6) * mm, "end": v(76.2, 64.77) * mm});
            skLineSegment(sketch, "E2.11.6.0", {"start": v(76.2, 58.42) * mm, "end": v(79.37, 58.42) * mm});
            skLineSegment(sketch, "E2.11.6.1", {"start": v(79.37, 55.25) * mm, "end": v(79.37, 58.42) * mm});
            skLineSegment(sketch, "E2.11.6.2", {"start": v(76.2, 55.25) * mm, "end": v(79.37, 55.25) * mm});
            skLineSegment(sketch, "E2.11.6.3", {"start": v(76.2, 55.25) * mm, "end": v(76.2, 58.42) * mm});
            skLineSegment(sketch, "E2.11.7.0", {"start": v(76.2, 52.07) * mm, "end": v(79.37, 52.07) * mm});
            skLineSegment(sketch, "E2.11.7.1", {"start": v(79.37, 48.9) * mm, "end": v(79.37, 52.07) * mm});
            skLineSegment(sketch, "E2.11.7.2", {"start": v(76.2, 48.9) * mm, "end": v(79.37, 48.9) * mm});
            skLineSegment(sketch, "E2.11.7.3", {"start": v(76.2, 48.9) * mm, "end": v(76.2, 52.07) * mm});
            skLineSegment(sketch, "E2.11.8.0", {"start": v(76.2, 45.72) * mm, "end": v(79.37, 45.72) * mm});
            skLineSegment(sketch, "E2.11.8.1", {"start": v(79.37, 42.55) * mm, "end": v(79.37, 45.72) * mm});
            skLineSegment(sketch, "E2.11.8.2", {"start": v(76.2, 42.55) * mm, "end": v(79.37, 42.55) * mm});
            skLineSegment(sketch, "E2.11.8.3", {"start": v(76.2, 42.55) * mm, "end": v(76.2, 45.72) * mm});
            skLineSegment(sketch, "E2.11.9.0", {"start": v(76.2, 39.37) * mm, "end": v(79.37, 39.37) * mm});
            skLineSegment(sketch, "E2.11.9.1", {"start": v(79.37, 36.2) * mm, "end": v(79.37, 39.37) * mm});
            skLineSegment(sketch, "E2.11.9.2", {"start": v(76.2, 36.2) * mm, "end": v(79.37, 36.2) * mm});
            skLineSegment(sketch, "E2.11.9.3", {"start": v(76.2, 36.2) * mm, "end": v(76.2, 39.37) * mm});
            skLineSegment(sketch, "E2.11.10.0", {"start": v(76.2, 33.02) * mm, "end": v(79.37, 33.02) * mm});
            skLineSegment(sketch, "E2.11.10.1", {"start": v(79.37, 29.85) * mm, "end": v(79.37, 33.02) * mm});
            skLineSegment(sketch, "E2.11.10.2", {"start": v(76.2, 29.85) * mm, "end": v(79.37, 29.85) * mm});
            skLineSegment(sketch, "E2.11.10.3", {"start": v(76.2, 29.85) * mm, "end": v(76.2, 33.02) * mm});
            skLineSegment(sketch, "E2.11.11.0", {"start": v(76.2, 26.67) * mm, "end": v(79.37, 26.67) * mm});
            skLineSegment(sketch, "E2.11.11.1", {"start": v(79.37, 23.5) * mm, "end": v(79.37, 26.67) * mm});
            skLineSegment(sketch, "E2.11.11.2", {"start": v(76.2, 23.5) * mm, "end": v(79.37, 23.5) * mm});
            skLineSegment(sketch, "E2.11.11.3", {"start": v(76.2, 23.5) * mm, "end": v(76.2, 26.67) * mm});
            skLineSegment(sketch, "E2.11.12.0", {"start": v(76.2, 20.32) * mm, "end": v(79.37, 20.32) * mm});
            skLineSegment(sketch, "E2.11.12.1", {"start": v(79.37, 17.15) * mm, "end": v(79.37, 20.32) * mm});
            skLineSegment(sketch, "E2.11.12.2", {"start": v(76.2, 17.15) * mm, "end": v(79.37, 17.15) * mm});
            skLineSegment(sketch, "E2.11.12.3", {"start": v(76.2, 17.15) * mm, "end": v(76.2, 20.32) * mm});
            skLineSegment(sketch, "E2.11.13.0", {"start": v(76.2, 13.97) * mm, "end": v(79.37, 13.97) * mm});
            skLineSegment(sketch, "E2.11.13.1", {"start": v(79.37, 10.8) * mm, "end": v(79.37, 13.97) * mm});
            skLineSegment(sketch, "E2.11.13.2", {"start": v(76.2, 10.8) * mm, "end": v(79.37, 10.8) * mm});
            skLineSegment(sketch, "E2.11.13.3", {"start": v(76.2, 10.8) * mm, "end": v(76.2, 13.97) * mm});
            skLineSegment(sketch, "E2.11.14.0", {"start": v(76.2, 7.62) * mm, "end": v(79.37, 7.62) * mm});
            skLineSegment(sketch, "E2.11.14.1", {"start": v(79.37, 4.45) * mm, "end": v(79.37, 7.62) * mm});
            skLineSegment(sketch, "E2.11.14.2", {"start": v(76.2, 4.45) * mm, "end": v(79.37, 4.45) * mm});
            skLineSegment(sketch, "E2.11.14.3", {"start": v(76.2, 4.45) * mm, "end": v(76.2, 7.62) * mm});
            skLineSegment(sketch, "E2.12.0.0", {"start": v(82.55, 96.52) * mm, "end": v(85.72, 96.52) * mm});
            skLineSegment(sketch, "E2.12.0.1", {"start": v(85.72, 93.35) * mm, "end": v(85.72, 96.52) * mm});
            skLineSegment(sketch, "E2.12.0.2", {"start": v(82.55, 93.35) * mm, "end": v(85.72, 93.35) * mm});
            skLineSegment(sketch, "E2.12.0.3", {"start": v(82.55, 93.35) * mm, "end": v(82.55, 96.52) * mm});
            skLineSegment(sketch, "E2.12.1.0", {"start": v(82.55, 90.17) * mm, "end": v(85.72, 90.17) * mm});
            skLineSegment(sketch, "E2.12.1.1", {"start": v(85.72, 87) * mm, "end": v(85.72, 90.17) * mm});
            skLineSegment(sketch, "E2.12.1.2", {"start": v(82.55, 87) * mm, "end": v(85.72, 87) * mm});
            skLineSegment(sketch, "E2.12.1.3", {"start": v(82.55, 87) * mm, "end": v(82.55, 90.17) * mm});
            skLineSegment(sketch, "E2.12.2.0", {"start": v(82.55, 83.82) * mm, "end": v(85.72, 83.82) * mm});
            skLineSegment(sketch, "E2.12.2.1", {"start": v(85.72, 80.65) * mm, "end": v(85.72, 83.82) * mm});
            skLineSegment(sketch, "E2.12.2.2", {"start": v(82.55, 80.65) * mm, "end": v(85.72, 80.65) * mm});
            skLineSegment(sketch, "E2.12.2.3", {"start": v(82.55, 80.65) * mm, "end": v(82.55, 83.82) * mm});
            skLineSegment(sketch, "E2.12.3.0", {"start": v(82.55, 77.47) * mm, "end": v(85.72, 77.47) * mm});
            skLineSegment(sketch, "E2.12.3.1", {"start": v(85.72, 74.3) * mm, "end": v(85.72, 77.47) * mm});
            skLineSegment(sketch, "E2.12.3.2", {"start": v(82.55, 74.3) * mm, "end": v(85.72, 74.3) * mm});
            skLineSegment(sketch, "E2.12.3.3", {"start": v(82.55, 74.3) * mm, "end": v(82.55, 77.47) * mm});
            skLineSegment(sketch, "E2.12.4.0", {"start": v(82.55, 71.12) * mm, "end": v(85.72, 71.12) * mm});
            skLineSegment(sketch, "E2.12.4.1", {"start": v(85.72, 67.95) * mm, "end": v(85.72, 71.12) * mm});
            skLineSegment(sketch, "E2.12.4.2", {"start": v(82.55, 67.95) * mm, "end": v(85.72, 67.95) * mm});
            skLineSegment(sketch, "E2.12.4.3", {"start": v(82.55, 67.95) * mm, "end": v(82.55, 71.12) * mm});
            skLineSegment(sketch, "E2.12.5.0", {"start": v(82.55, 64.77) * mm, "end": v(85.72, 64.77) * mm});
            skLineSegment(sketch, "E2.12.5.1", {"start": v(85.72, 61.6) * mm, "end": v(85.72, 64.77) * mm});
            skLineSegment(sketch, "E2.12.5.2", {"start": v(82.55, 61.6) * mm, "end": v(85.72, 61.6) * mm});
            skLineSegment(sketch, "E2.12.5.3", {"start": v(82.55, 61.6) * mm, "end": v(82.55, 64.77) * mm});
            skLineSegment(sketch, "E2.12.6.0", {"start": v(82.55, 58.42) * mm, "end": v(85.72, 58.42) * mm});
            skLineSegment(sketch, "E2.12.6.1", {"start": v(85.72, 55.25) * mm, "end": v(85.72, 58.42) * mm});
            skLineSegment(sketch, "E2.12.6.2", {"start": v(82.55, 55.25) * mm, "end": v(85.72, 55.25) * mm});
            skLineSegment(sketch, "E2.12.6.3", {"start": v(82.55, 55.25) * mm, "end": v(82.55, 58.42) * mm});
            skLineSegment(sketch, "E2.12.7.0", {"start": v(82.55, 52.07) * mm, "end": v(85.72, 52.07) * mm});
            skLineSegment(sketch, "E2.12.7.1", {"start": v(85.72, 48.9) * mm, "end": v(85.72, 52.07) * mm});
            skLineSegment(sketch, "E2.12.7.2", {"start": v(82.55, 48.9) * mm, "end": v(85.72, 48.9) * mm});
            skLineSegment(sketch, "E2.12.7.3", {"start": v(82.55, 48.9) * mm, "end": v(82.55, 52.07) * mm});
            skLineSegment(sketch, "E2.12.8.0", {"start": v(82.55, 45.72) * mm, "end": v(85.72, 45.72) * mm});
            skLineSegment(sketch, "E2.12.8.1", {"start": v(85.72, 42.55) * mm, "end": v(85.72, 45.72) * mm});
            skLineSegment(sketch, "E2.12.8.2", {"start": v(82.55, 42.55) * mm, "end": v(85.72, 42.55) * mm});
            skLineSegment(sketch, "E2.12.8.3", {"start": v(82.55, 42.55) * mm, "end": v(82.55, 45.72) * mm});
            skLineSegment(sketch, "E2.12.9.0", {"start": v(82.55, 39.37) * mm, "end": v(85.72, 39.37) * mm});
            skLineSegment(sketch, "E2.12.9.1", {"start": v(85.72, 36.2) * mm, "end": v(85.72, 39.37) * mm});
            skLineSegment(sketch, "E2.12.9.2", {"start": v(82.55, 36.2) * mm, "end": v(85.72, 36.2) * mm});
            skLineSegment(sketch, "E2.12.9.3", {"start": v(82.55, 36.2) * mm, "end": v(82.55, 39.37) * mm});
            skLineSegment(sketch, "E2.12.10.0", {"start": v(82.55, 33.02) * mm, "end": v(85.72, 33.02) * mm});
            skLineSegment(sketch, "E2.12.10.1", {"start": v(85.72, 29.85) * mm, "end": v(85.72, 33.02) * mm});
            skLineSegment(sketch, "E2.12.10.2", {"start": v(82.55, 29.85) * mm, "end": v(85.72, 29.85) * mm});
            skLineSegment(sketch, "E2.12.10.3", {"start": v(82.55, 29.85) * mm, "end": v(82.55, 33.02) * mm});
            skLineSegment(sketch, "E2.12.11.0", {"start": v(82.55, 26.67) * mm, "end": v(85.72, 26.67) * mm});
            skLineSegment(sketch, "E2.12.11.1", {"start": v(85.72, 23.5) * mm, "end": v(85.72, 26.67) * mm});
            skLineSegment(sketch, "E2.12.11.2", {"start": v(82.55, 23.5) * mm, "end": v(85.72, 23.5) * mm});
            skLineSegment(sketch, "E2.12.11.3", {"start": v(82.55, 23.5) * mm, "end": v(82.55, 26.67) * mm});
            skLineSegment(sketch, "E2.12.12.0", {"start": v(82.55, 20.32) * mm, "end": v(85.72, 20.32) * mm});
            skLineSegment(sketch, "E2.12.12.1", {"start": v(85.72, 17.15) * mm, "end": v(85.72, 20.32) * mm});
            skLineSegment(sketch, "E2.12.12.2", {"start": v(82.55, 17.15) * mm, "end": v(85.72, 17.15) * mm});
            skLineSegment(sketch, "E2.12.12.3", {"start": v(82.55, 17.15) * mm, "end": v(82.55, 20.32) * mm});
            skLineSegment(sketch, "E2.12.13.0", {"start": v(82.55, 13.97) * mm, "end": v(85.72, 13.97) * mm});
            skLineSegment(sketch, "E2.12.13.1", {"start": v(85.72, 10.8) * mm, "end": v(85.72, 13.97) * mm});
            skLineSegment(sketch, "E2.12.13.2", {"start": v(82.55, 10.8) * mm, "end": v(85.72, 10.8) * mm});
            skLineSegment(sketch, "E2.12.13.3", {"start": v(82.55, 10.8) * mm, "end": v(82.55, 13.97) * mm});
            skLineSegment(sketch, "E2.12.14.0", {"start": v(82.55, 7.62) * mm, "end": v(85.72, 7.62) * mm});
            skLineSegment(sketch, "E2.12.14.1", {"start": v(85.72, 4.45) * mm, "end": v(85.72, 7.62) * mm});
            skLineSegment(sketch, "E2.12.14.2", {"start": v(82.55, 4.45) * mm, "end": v(85.72, 4.45) * mm});
            skLineSegment(sketch, "E2.12.14.3", {"start": v(82.55, 4.45) * mm, "end": v(82.55, 7.62) * mm});
            skLineSegment(sketch, "E2.13.0.0", {"start": v(88.9, 96.52) * mm, "end": v(92.07, 96.52) * mm});
            skLineSegment(sketch, "E2.13.0.1", {"start": v(92.07, 93.35) * mm, "end": v(92.07, 96.52) * mm});
            skLineSegment(sketch, "E2.13.0.2", {"start": v(88.9, 93.35) * mm, "end": v(92.07, 93.35) * mm});
            skLineSegment(sketch, "E2.13.0.3", {"start": v(88.9, 93.35) * mm, "end": v(88.9, 96.52) * mm});
            skLineSegment(sketch, "E2.13.1.0", {"start": v(88.9, 90.17) * mm, "end": v(92.07, 90.17) * mm});
            skLineSegment(sketch, "E2.13.1.1", {"start": v(92.07, 87) * mm, "end": v(92.07, 90.17) * mm});
            skLineSegment(sketch, "E2.13.1.2", {"start": v(88.9, 87) * mm, "end": v(92.07, 87) * mm});
            skLineSegment(sketch, "E2.13.1.3", {"start": v(88.9, 87) * mm, "end": v(88.9, 90.17) * mm});
            skLineSegment(sketch, "E2.13.2.0", {"start": v(88.9, 83.82) * mm, "end": v(92.07, 83.82) * mm});
            skLineSegment(sketch, "E2.13.2.1", {"start": v(92.07, 80.65) * mm, "end": v(92.07, 83.82) * mm});
            skLineSegment(sketch, "E2.13.2.2", {"start": v(88.9, 80.65) * mm, "end": v(92.07, 80.65) * mm});
            skLineSegment(sketch, "E2.13.2.3", {"start": v(88.9, 80.65) * mm, "end": v(88.9, 83.82) * mm});
            skLineSegment(sketch, "E2.13.3.0", {"start": v(88.9, 77.47) * mm, "end": v(92.07, 77.47) * mm});
            skLineSegment(sketch, "E2.13.3.1", {"start": v(92.07, 74.3) * mm, "end": v(92.07, 77.47) * mm});
            skLineSegment(sketch, "E2.13.3.2", {"start": v(88.9, 74.3) * mm, "end": v(92.07, 74.3) * mm});
            skLineSegment(sketch, "E2.13.3.3", {"start": v(88.9, 74.3) * mm, "end": v(88.9, 77.47) * mm});
            skLineSegment(sketch, "E2.13.4.0", {"start": v(88.9, 71.12) * mm, "end": v(92.07, 71.12) * mm});
            skLineSegment(sketch, "E2.13.4.1", {"start": v(92.07, 67.95) * mm, "end": v(92.07, 71.12) * mm});
            skLineSegment(sketch, "E2.13.4.2", {"start": v(88.9, 67.95) * mm, "end": v(92.07, 67.95) * mm});
            skLineSegment(sketch, "E2.13.4.3", {"start": v(88.9, 67.95) * mm, "end": v(88.9, 71.12) * mm});
            skLineSegment(sketch, "E2.13.5.0", {"start": v(88.9, 64.77) * mm, "end": v(92.07, 64.77) * mm});
            skLineSegment(sketch, "E2.13.5.1", {"start": v(92.07, 61.6) * mm, "end": v(92.07, 64.77) * mm});
            skLineSegment(sketch, "E2.13.5.2", {"start": v(88.9, 61.6) * mm, "end": v(92.07, 61.6) * mm});
            skLineSegment(sketch, "E2.13.5.3", {"start": v(88.9, 61.6) * mm, "end": v(88.9, 64.77) * mm});
            skLineSegment(sketch, "E2.13.6.0", {"start": v(88.9, 58.42) * mm, "end": v(92.07, 58.42) * mm});
            skLineSegment(sketch, "E2.13.6.1", {"start": v(92.07, 55.25) * mm, "end": v(92.07, 58.42) * mm});
            skLineSegment(sketch, "E2.13.6.2", {"start": v(88.9, 55.25) * mm, "end": v(92.07, 55.25) * mm});
            skLineSegment(sketch, "E2.13.6.3", {"start": v(88.9, 55.25) * mm, "end": v(88.9, 58.42) * mm});
            skLineSegment(sketch, "E2.13.7.0", {"start": v(88.9, 52.07) * mm, "end": v(92.07, 52.07) * mm});
            skLineSegment(sketch, "E2.13.7.1", {"start": v(92.07, 48.9) * mm, "end": v(92.07, 52.07) * mm});
            skLineSegment(sketch, "E2.13.7.2", {"start": v(88.9, 48.9) * mm, "end": v(92.07, 48.9) * mm});
            skLineSegment(sketch, "E2.13.7.3", {"start": v(88.9, 48.9) * mm, "end": v(88.9, 52.07) * mm});
            skLineSegment(sketch, "E2.13.8.0", {"start": v(88.9, 45.72) * mm, "end": v(92.07, 45.72) * mm});
            skLineSegment(sketch, "E2.13.8.1", {"start": v(92.07, 42.55) * mm, "end": v(92.07, 45.72) * mm});
            skLineSegment(sketch, "E2.13.8.2", {"start": v(88.9, 42.55) * mm, "end": v(92.07, 42.55) * mm});
            skLineSegment(sketch, "E2.13.8.3", {"start": v(88.9, 42.55) * mm, "end": v(88.9, 45.72) * mm});
            skLineSegment(sketch, "E2.13.9.0", {"start": v(88.9, 39.37) * mm, "end": v(92.07, 39.37) * mm});
            skLineSegment(sketch, "E2.13.9.1", {"start": v(92.07, 36.2) * mm, "end": v(92.07, 39.37) * mm});
            skLineSegment(sketch, "E2.13.9.2", {"start": v(88.9, 36.2) * mm, "end": v(92.07, 36.2) * mm});
            skLineSegment(sketch, "E2.13.9.3", {"start": v(88.9, 36.2) * mm, "end": v(88.9, 39.37) * mm});
            skLineSegment(sketch, "E2.13.10.0", {"start": v(88.9, 33.02) * mm, "end": v(92.07, 33.02) * mm});
            skLineSegment(sketch, "E2.13.10.1", {"start": v(92.07, 29.85) * mm, "end": v(92.07, 33.02) * mm});
            skLineSegment(sketch, "E2.13.10.2", {"start": v(88.9, 29.85) * mm, "end": v(92.07, 29.85) * mm});
            skLineSegment(sketch, "E2.13.10.3", {"start": v(88.9, 29.85) * mm, "end": v(88.9, 33.02) * mm});
            skLineSegment(sketch, "E2.13.11.0", {"start": v(88.9, 26.67) * mm, "end": v(92.07, 26.67) * mm});
            skLineSegment(sketch, "E2.13.11.1", {"start": v(92.07, 23.5) * mm, "end": v(92.07, 26.67) * mm});
            skLineSegment(sketch, "E2.13.11.2", {"start": v(88.9, 23.5) * mm, "end": v(92.07, 23.5) * mm});
            skLineSegment(sketch, "E2.13.11.3", {"start": v(88.9, 23.5) * mm, "end": v(88.9, 26.67) * mm});
            skLineSegment(sketch, "E2.13.12.0", {"start": v(88.9, 20.32) * mm, "end": v(92.07, 20.32) * mm});
            skLineSegment(sketch, "E2.13.12.1", {"start": v(92.07, 17.15) * mm, "end": v(92.07, 20.32) * mm});
            skLineSegment(sketch, "E2.13.12.2", {"start": v(88.9, 17.15) * mm, "end": v(92.07, 17.15) * mm});
            skLineSegment(sketch, "E2.13.12.3", {"start": v(88.9, 17.15) * mm, "end": v(88.9, 20.32) * mm});
            skLineSegment(sketch, "E2.13.13.0", {"start": v(88.9, 13.97) * mm, "end": v(92.07, 13.97) * mm});
            skLineSegment(sketch, "E2.13.13.1", {"start": v(92.07, 10.8) * mm, "end": v(92.07, 13.97) * mm});
            skLineSegment(sketch, "E2.13.13.2", {"start": v(88.9, 10.8) * mm, "end": v(92.07, 10.8) * mm});
            skLineSegment(sketch, "E2.13.13.3", {"start": v(88.9, 10.8) * mm, "end": v(88.9, 13.97) * mm});
            skLineSegment(sketch, "E2.13.14.0", {"start": v(88.9, 7.62) * mm, "end": v(92.07, 7.62) * mm});
            skLineSegment(sketch, "E2.13.14.1", {"start": v(92.07, 4.45) * mm, "end": v(92.07, 7.62) * mm});
            skLineSegment(sketch, "E2.13.14.2", {"start": v(88.9, 4.45) * mm, "end": v(92.07, 4.45) * mm});
            skLineSegment(sketch, "E2.13.14.3", {"start": v(88.9, 4.45) * mm, "end": v(88.9, 7.62) * mm});
            skLineSegment(sketch, "E2.14.0.0", {"start": v(95.25, 96.52) * mm, "end": v(98.42, 96.52) * mm});
            skLineSegment(sketch, "E2.14.0.1", {"start": v(98.42, 93.35) * mm, "end": v(98.42, 96.52) * mm});
            skLineSegment(sketch, "E2.14.0.2", {"start": v(95.25, 93.35) * mm, "end": v(98.42, 93.35) * mm});
            skLineSegment(sketch, "E2.14.0.3", {"start": v(95.25, 93.35) * mm, "end": v(95.25, 96.52) * mm});
            skLineSegment(sketch, "E2.14.1.0", {"start": v(95.25, 90.17) * mm, "end": v(98.42, 90.17) * mm});
            skLineSegment(sketch, "E2.14.1.1", {"start": v(98.42, 87) * mm, "end": v(98.42, 90.17) * mm});
            skLineSegment(sketch, "E2.14.1.2", {"start": v(95.25, 87) * mm, "end": v(98.42, 87) * mm});
            skLineSegment(sketch, "E2.14.1.3", {"start": v(95.25, 87) * mm, "end": v(95.25, 90.17) * mm});
            skLineSegment(sketch, "E2.14.2.0", {"start": v(95.25, 83.82) * mm, "end": v(98.42, 83.82) * mm});
            skLineSegment(sketch, "E2.14.2.1", {"start": v(98.42, 80.65) * mm, "end": v(98.42, 83.82) * mm});
            skLineSegment(sketch, "E2.14.2.2", {"start": v(95.25, 80.65) * mm, "end": v(98.42, 80.65) * mm});
            skLineSegment(sketch, "E2.14.2.3", {"start": v(95.25, 80.65) * mm, "end": v(95.25, 83.82) * mm});
            skLineSegment(sketch, "E2.14.3.0", {"start": v(95.25, 77.47) * mm, "end": v(98.42, 77.47) * mm});
            skLineSegment(sketch, "E2.14.3.1", {"start": v(98.42, 74.3) * mm, "end": v(98.42, 77.47) * mm});
            skLineSegment(sketch, "E2.14.3.2", {"start": v(95.25, 74.3) * mm, "end": v(98.42, 74.3) * mm});
            skLineSegment(sketch, "E2.14.3.3", {"start": v(95.25, 74.3) * mm, "end": v(95.25, 77.47) * mm});
            skLineSegment(sketch, "E2.14.4.0", {"start": v(95.25, 71.12) * mm, "end": v(98.42, 71.12) * mm});
            skLineSegment(sketch, "E2.14.4.1", {"start": v(98.42, 67.95) * mm, "end": v(98.42, 71.12) * mm});
            skLineSegment(sketch, "E2.14.4.2", {"start": v(95.25, 67.95) * mm, "end": v(98.42, 67.95) * mm});
            skLineSegment(sketch, "E2.14.4.3", {"start": v(95.25, 67.95) * mm, "end": v(95.25, 71.12) * mm});
            skLineSegment(sketch, "E2.14.5.0", {"start": v(95.25, 64.77) * mm, "end": v(98.42, 64.77) * mm});
            skLineSegment(sketch, "E2.14.5.1", {"start": v(98.42, 61.6) * mm, "end": v(98.42, 64.77) * mm});
            skLineSegment(sketch, "E2.14.5.2", {"start": v(95.25, 61.6) * mm, "end": v(98.42, 61.6) * mm});
            skLineSegment(sketch, "E2.14.5.3", {"start": v(95.25, 61.6) * mm, "end": v(95.25, 64.77) * mm});
            skLineSegment(sketch, "E2.14.6.0", {"start": v(95.25, 58.42) * mm, "end": v(98.42, 58.42) * mm});
            skLineSegment(sketch, "E2.14.6.1", {"start": v(98.42, 55.25) * mm, "end": v(98.42, 58.42) * mm});
            skLineSegment(sketch, "E2.14.6.2", {"start": v(95.25, 55.25) * mm, "end": v(98.42, 55.25) * mm});
            skLineSegment(sketch, "E2.14.6.3", {"start": v(95.25, 55.25) * mm, "end": v(95.25, 58.42) * mm});
            skLineSegment(sketch, "E2.14.7.0", {"start": v(95.25, 52.07) * mm, "end": v(98.42, 52.07) * mm});
            skLineSegment(sketch, "E2.14.7.1", {"start": v(98.42, 48.9) * mm, "end": v(98.42, 52.07) * mm});
            skLineSegment(sketch, "E2.14.7.2", {"start": v(95.25, 48.9) * mm, "end": v(98.42, 48.9) * mm});
            skLineSegment(sketch, "E2.14.7.3", {"start": v(95.25, 48.9) * mm, "end": v(95.25, 52.07) * mm});
            skLineSegment(sketch, "E2.14.8.0", {"start": v(95.25, 45.72) * mm, "end": v(98.42, 45.72) * mm});
            skLineSegment(sketch, "E2.14.8.1", {"start": v(98.42, 42.55) * mm, "end": v(98.42, 45.72) * mm});
            skLineSegment(sketch, "E2.14.8.2", {"start": v(95.25, 42.55) * mm, "end": v(98.42, 42.55) * mm});
            skLineSegment(sketch, "E2.14.8.3", {"start": v(95.25, 42.55) * mm, "end": v(95.25, 45.72) * mm});
            skLineSegment(sketch, "E2.14.9.0", {"start": v(95.25, 39.37) * mm, "end": v(98.42, 39.37) * mm});
            skLineSegment(sketch, "E2.14.9.1", {"start": v(98.42, 36.2) * mm, "end": v(98.42, 39.37) * mm});
            skLineSegment(sketch, "E2.14.9.2", {"start": v(95.25, 36.2) * mm, "end": v(98.42, 36.2) * mm});
            skLineSegment(sketch, "E2.14.9.3", {"start": v(95.25, 36.2) * mm, "end": v(95.25, 39.37) * mm});
            skLineSegment(sketch, "E2.14.10.0", {"start": v(95.25, 33.02) * mm, "end": v(98.42, 33.02) * mm});
            skLineSegment(sketch, "E2.14.10.1", {"start": v(98.42, 29.85) * mm, "end": v(98.42, 33.02) * mm});
            skLineSegment(sketch, "E2.14.10.2", {"start": v(95.25, 29.85) * mm, "end": v(98.42, 29.85) * mm});
            skLineSegment(sketch, "E2.14.10.3", {"start": v(95.25, 29.85) * mm, "end": v(95.25, 33.02) * mm});
            skLineSegment(sketch, "E2.14.11.0", {"start": v(95.25, 26.67) * mm, "end": v(98.42, 26.67) * mm});
            skLineSegment(sketch, "E2.14.11.1", {"start": v(98.42, 23.5) * mm, "end": v(98.42, 26.67) * mm});
            skLineSegment(sketch, "E2.14.11.2", {"start": v(95.25, 23.5) * mm, "end": v(98.42, 23.5) * mm});
            skLineSegment(sketch, "E2.14.11.3", {"start": v(95.25, 23.5) * mm, "end": v(95.25, 26.67) * mm});
            skLineSegment(sketch, "E2.14.12.0", {"start": v(95.25, 20.32) * mm, "end": v(98.42, 20.32) * mm});
            skLineSegment(sketch, "E2.14.12.1", {"start": v(98.42, 17.15) * mm, "end": v(98.42, 20.32) * mm});
            skLineSegment(sketch, "E2.14.12.2", {"start": v(95.25, 17.15) * mm, "end": v(98.42, 17.15) * mm});
            skLineSegment(sketch, "E2.14.12.3", {"start": v(95.25, 17.15) * mm, "end": v(95.25, 20.32) * mm});
            skLineSegment(sketch, "E2.14.13.0", {"start": v(95.25, 13.97) * mm, "end": v(98.42, 13.97) * mm});
            skLineSegment(sketch, "E2.14.13.1", {"start": v(98.42, 10.8) * mm, "end": v(98.42, 13.97) * mm});
            skLineSegment(sketch, "E2.14.13.2", {"start": v(95.25, 10.8) * mm, "end": v(98.42, 10.8) * mm});
            skLineSegment(sketch, "E2.14.13.3", {"start": v(95.25, 10.8) * mm, "end": v(95.25, 13.97) * mm});
            skLineSegment(sketch, "E2.14.14.0", {"start": v(95.25, 7.62) * mm, "end": v(98.42, 7.62) * mm});
            skLineSegment(sketch, "E2.14.14.1", {"start": v(98.42, 4.45) * mm, "end": v(98.42, 7.62) * mm});
            skLineSegment(sketch, "E2.14.14.2", {"start": v(95.25, 4.45) * mm, "end": v(98.42, 4.45) * mm});
            skLineSegment(sketch, "E2.14.14.3", {"start": v(95.25, 4.45) * mm, "end": v(95.25, 7.62) * mm});
            skLineSegment(sketch, "E2.15.0.0", {"start": v(101.6, 96.52) * mm, "end": v(104.77, 96.52) * mm});
            skLineSegment(sketch, "E2.15.0.1", {"start": v(104.77, 93.35) * mm, "end": v(104.77, 96.52) * mm});
            skLineSegment(sketch, "E2.15.0.2", {"start": v(101.6, 93.35) * mm, "end": v(104.77, 93.35) * mm});
            skLineSegment(sketch, "E2.15.0.3", {"start": v(101.6, 93.35) * mm, "end": v(101.6, 96.52) * mm});
            skLineSegment(sketch, "E2.15.1.0", {"start": v(101.6, 90.17) * mm, "end": v(104.77, 90.17) * mm});
            skLineSegment(sketch, "E2.15.1.1", {"start": v(104.77, 87) * mm, "end": v(104.77, 90.17) * mm});
            skLineSegment(sketch, "E2.15.1.2", {"start": v(101.6, 87) * mm, "end": v(104.77, 87) * mm});
            skLineSegment(sketch, "E2.15.1.3", {"start": v(101.6, 87) * mm, "end": v(101.6, 90.17) * mm});
            skLineSegment(sketch, "E2.15.2.0", {"start": v(101.6, 83.82) * mm, "end": v(104.77, 83.82) * mm});
            skLineSegment(sketch, "E2.15.2.1", {"start": v(104.77, 80.65) * mm, "end": v(104.77, 83.82) * mm});
            skLineSegment(sketch, "E2.15.2.2", {"start": v(101.6, 80.65) * mm, "end": v(104.77, 80.65) * mm});
            skLineSegment(sketch, "E2.15.2.3", {"start": v(101.6, 80.65) * mm, "end": v(101.6, 83.82) * mm});
            skLineSegment(sketch, "E2.15.3.0", {"start": v(101.6, 77.47) * mm, "end": v(104.77, 77.47) * mm});
            skLineSegment(sketch, "E2.15.3.1", {"start": v(104.77, 74.3) * mm, "end": v(104.77, 77.47) * mm});
            skLineSegment(sketch, "E2.15.3.2", {"start": v(101.6, 74.3) * mm, "end": v(104.77, 74.3) * mm});
            skLineSegment(sketch, "E2.15.3.3", {"start": v(101.6, 74.3) * mm, "end": v(101.6, 77.47) * mm});
            skLineSegment(sketch, "E2.15.4.0", {"start": v(101.6, 71.12) * mm, "end": v(104.77, 71.12) * mm});
            skLineSegment(sketch, "E2.15.4.1", {"start": v(104.77, 67.95) * mm, "end": v(104.77, 71.12) * mm});
            skLineSegment(sketch, "E2.15.4.2", {"start": v(101.6, 67.95) * mm, "end": v(104.77, 67.95) * mm});
            skLineSegment(sketch, "E2.15.4.3", {"start": v(101.6, 67.95) * mm, "end": v(101.6, 71.12) * mm});
            skLineSegment(sketch, "E2.15.5.0", {"start": v(101.6, 64.77) * mm, "end": v(104.77, 64.77) * mm});
            skLineSegment(sketch, "E2.15.5.1", {"start": v(104.77, 61.6) * mm, "end": v(104.77, 64.77) * mm});
            skLineSegment(sketch, "E2.15.5.2", {"start": v(101.6, 61.6) * mm, "end": v(104.77, 61.6) * mm});
            skLineSegment(sketch, "E2.15.5.3", {"start": v(101.6, 61.6) * mm, "end": v(101.6, 64.77) * mm});
            skLineSegment(sketch, "E2.15.6.0", {"start": v(101.6, 58.42) * mm, "end": v(104.77, 58.42) * mm});
            skLineSegment(sketch, "E2.15.6.1", {"start": v(104.77, 55.25) * mm, "end": v(104.77, 58.42) * mm});
            skLineSegment(sketch, "E2.15.6.2", {"start": v(101.6, 55.25) * mm, "end": v(104.77, 55.25) * mm});
            skLineSegment(sketch, "E2.15.6.3", {"start": v(101.6, 55.25) * mm, "end": v(101.6, 58.42) * mm});
            skLineSegment(sketch, "E2.15.7.0", {"start": v(101.6, 52.07) * mm, "end": v(104.77, 52.07) * mm});
            skLineSegment(sketch, "E2.15.7.1", {"start": v(104.77, 48.9) * mm, "end": v(104.77, 52.07) * mm});
            skLineSegment(sketch, "E2.15.7.2", {"start": v(101.6, 48.9) * mm, "end": v(104.77, 48.9) * mm});
            skLineSegment(sketch, "E2.15.7.3", {"start": v(101.6, 48.9) * mm, "end": v(101.6, 52.07) * mm});
            skLineSegment(sketch, "E2.15.8.0", {"start": v(101.6, 45.72) * mm, "end": v(104.77, 45.72) * mm});
            skLineSegment(sketch, "E2.15.8.1", {"start": v(104.77, 42.55) * mm, "end": v(104.77, 45.72) * mm});
            skLineSegment(sketch, "E2.15.8.2", {"start": v(101.6, 42.55) * mm, "end": v(104.77, 42.55) * mm});
            skLineSegment(sketch, "E2.15.8.3", {"start": v(101.6, 42.55) * mm, "end": v(101.6, 45.72) * mm});
            skLineSegment(sketch, "E2.15.9.0", {"start": v(101.6, 39.37) * mm, "end": v(104.77, 39.37) * mm});
            skLineSegment(sketch, "E2.15.9.1", {"start": v(104.77, 36.2) * mm, "end": v(104.77, 39.37) * mm});
            skLineSegment(sketch, "E2.15.9.2", {"start": v(101.6, 36.2) * mm, "end": v(104.77, 36.2) * mm});
            skLineSegment(sketch, "E2.15.9.3", {"start": v(101.6, 36.2) * mm, "end": v(101.6, 39.37) * mm});
            skLineSegment(sketch, "E2.15.10.0", {"start": v(101.6, 33.02) * mm, "end": v(104.77, 33.02) * mm});
            skLineSegment(sketch, "E2.15.10.1", {"start": v(104.77, 29.85) * mm, "end": v(104.77, 33.02) * mm});
            skLineSegment(sketch, "E2.15.10.2", {"start": v(101.6, 29.85) * mm, "end": v(104.77, 29.85) * mm});
            skLineSegment(sketch, "E2.15.10.3", {"start": v(101.6, 29.85) * mm, "end": v(101.6, 33.02) * mm});
            skLineSegment(sketch, "E2.15.11.0", {"start": v(101.6, 26.67) * mm, "end": v(104.77, 26.67) * mm});
            skLineSegment(sketch, "E2.15.11.1", {"start": v(104.77, 23.5) * mm, "end": v(104.77, 26.67) * mm});
            skLineSegment(sketch, "E2.15.11.2", {"start": v(101.6, 23.5) * mm, "end": v(104.77, 23.5) * mm});
            skLineSegment(sketch, "E2.15.11.3", {"start": v(101.6, 23.5) * mm, "end": v(101.6, 26.67) * mm});
            skLineSegment(sketch, "E2.15.12.0", {"start": v(101.6, 20.32) * mm, "end": v(104.77, 20.32) * mm});
            skLineSegment(sketch, "E2.15.12.1", {"start": v(104.77, 17.15) * mm, "end": v(104.77, 20.32) * mm});
            skLineSegment(sketch, "E2.15.12.2", {"start": v(101.6, 17.15) * mm, "end": v(104.77, 17.15) * mm});
            skLineSegment(sketch, "E2.15.12.3", {"start": v(101.6, 17.15) * mm, "end": v(101.6, 20.32) * mm});
            skLineSegment(sketch, "E2.15.13.0", {"start": v(101.6, 13.97) * mm, "end": v(104.77, 13.97) * mm});
            skLineSegment(sketch, "E2.15.13.1", {"start": v(104.77, 10.8) * mm, "end": v(104.77, 13.97) * mm});
            skLineSegment(sketch, "E2.15.13.2", {"start": v(101.6, 10.8) * mm, "end": v(104.77, 10.8) * mm});
            skLineSegment(sketch, "E2.15.13.3", {"start": v(101.6, 10.8) * mm, "end": v(101.6, 13.97) * mm});
            skLineSegment(sketch, "E2.15.14.0", {"start": v(101.6, 7.62) * mm, "end": v(104.77, 7.62) * mm});
            skLineSegment(sketch, "E2.15.14.1", {"start": v(104.77, 4.45) * mm, "end": v(104.77, 7.62) * mm});
            skLineSegment(sketch, "E2.15.14.2", {"start": v(101.6, 4.45) * mm, "end": v(104.77, 4.45) * mm});
            skLineSegment(sketch, "E2.15.14.3", {"start": v(101.6, 4.45) * mm, "end": v(101.6, 7.62) * mm});
            skLineSegment(sketch, "E2.16.0.0", {"start": v(107.95, 96.52) * mm, "end": v(111.12, 96.52) * mm});
            skLineSegment(sketch, "E2.16.0.1", {"start": v(111.12, 93.35) * mm, "end": v(111.12, 96.52) * mm});
            skLineSegment(sketch, "E2.16.0.2", {"start": v(107.95, 93.35) * mm, "end": v(111.12, 93.35) * mm});
            skLineSegment(sketch, "E2.16.0.3", {"start": v(107.95, 93.35) * mm, "end": v(107.95, 96.52) * mm});
            skLineSegment(sketch, "E2.16.1.0", {"start": v(107.95, 90.17) * mm, "end": v(111.12, 90.17) * mm});
            skLineSegment(sketch, "E2.16.1.1", {"start": v(111.12, 87) * mm, "end": v(111.12, 90.17) * mm});
            skLineSegment(sketch, "E2.16.1.2", {"start": v(107.95, 87) * mm, "end": v(111.12, 87) * mm});
            skLineSegment(sketch, "E2.16.1.3", {"start": v(107.95, 87) * mm, "end": v(107.95, 90.17) * mm});
            skLineSegment(sketch, "E2.16.2.0", {"start": v(107.95, 83.82) * mm, "end": v(111.12, 83.82) * mm});
            skLineSegment(sketch, "E2.16.2.1", {"start": v(111.12, 80.65) * mm, "end": v(111.12, 83.82) * mm});
            skLineSegment(sketch, "E2.16.2.2", {"start": v(107.95, 80.65) * mm, "end": v(111.12, 80.65) * mm});
            skLineSegment(sketch, "E2.16.2.3", {"start": v(107.95, 80.65) * mm, "end": v(107.95, 83.82) * mm});
            skLineSegment(sketch, "E2.16.3.0", {"start": v(107.95, 77.47) * mm, "end": v(111.12, 77.47) * mm});
            skLineSegment(sketch, "E2.16.3.1", {"start": v(111.12, 74.3) * mm, "end": v(111.12, 77.47) * mm});
            skLineSegment(sketch, "E2.16.3.2", {"start": v(107.95, 74.3) * mm, "end": v(111.12, 74.3) * mm});
            skLineSegment(sketch, "E2.16.3.3", {"start": v(107.95, 74.3) * mm, "end": v(107.95, 77.47) * mm});
            skLineSegment(sketch, "E2.16.4.0", {"start": v(107.95, 71.12) * mm, "end": v(111.12, 71.12) * mm});
            skLineSegment(sketch, "E2.16.4.1", {"start": v(111.12, 67.95) * mm, "end": v(111.12, 71.12) * mm});
            skLineSegment(sketch, "E2.16.4.2", {"start": v(107.95, 67.95) * mm, "end": v(111.12, 67.95) * mm});
            skLineSegment(sketch, "E2.16.4.3", {"start": v(107.95, 67.95) * mm, "end": v(107.95, 71.12) * mm});
            skLineSegment(sketch, "E2.16.5.0", {"start": v(107.95, 64.77) * mm, "end": v(111.12, 64.77) * mm});
            skLineSegment(sketch, "E2.16.5.1", {"start": v(111.12, 61.6) * mm, "end": v(111.12, 64.77) * mm});
            skLineSegment(sketch, "E2.16.5.2", {"start": v(107.95, 61.6) * mm, "end": v(111.12, 61.6) * mm});
            skLineSegment(sketch, "E2.16.5.3", {"start": v(107.95, 61.6) * mm, "end": v(107.95, 64.77) * mm});
            skLineSegment(sketch, "E2.16.6.0", {"start": v(107.95, 58.42) * mm, "end": v(111.12, 58.42) * mm});
            skLineSegment(sketch, "E2.16.6.1", {"start": v(111.12, 55.25) * mm, "end": v(111.12, 58.42) * mm});
            skLineSegment(sketch, "E2.16.6.2", {"start": v(107.95, 55.25) * mm, "end": v(111.12, 55.25) * mm});
            skLineSegment(sketch, "E2.16.6.3", {"start": v(107.95, 55.25) * mm, "end": v(107.95, 58.42) * mm});
            skLineSegment(sketch, "E2.16.7.0", {"start": v(107.95, 52.07) * mm, "end": v(111.12, 52.07) * mm});
            skLineSegment(sketch, "E2.16.7.1", {"start": v(111.12, 48.9) * mm, "end": v(111.12, 52.07) * mm});
            skLineSegment(sketch, "E2.16.7.2", {"start": v(107.95, 48.9) * mm, "end": v(111.12, 48.9) * mm});
            skLineSegment(sketch, "E2.16.7.3", {"start": v(107.95, 48.9) * mm, "end": v(107.95, 52.07) * mm});
            skLineSegment(sketch, "E2.16.8.0", {"start": v(107.95, 45.72) * mm, "end": v(111.12, 45.72) * mm});
            skLineSegment(sketch, "E2.16.8.1", {"start": v(111.12, 42.55) * mm, "end": v(111.12, 45.72) * mm});
            skLineSegment(sketch, "E2.16.8.2", {"start": v(107.95, 42.55) * mm, "end": v(111.12, 42.55) * mm});
            skLineSegment(sketch, "E2.16.8.3", {"start": v(107.95, 42.55) * mm, "end": v(107.95, 45.72) * mm});
            skLineSegment(sketch, "E2.16.9.0", {"start": v(107.95, 39.37) * mm, "end": v(111.12, 39.37) * mm});
            skLineSegment(sketch, "E2.16.9.1", {"start": v(111.12, 36.2) * mm, "end": v(111.12, 39.37) * mm});
            skLineSegment(sketch, "E2.16.9.2", {"start": v(107.95, 36.2) * mm, "end": v(111.12, 36.2) * mm});
            skLineSegment(sketch, "E2.16.9.3", {"start": v(107.95, 36.2) * mm, "end": v(107.95, 39.37) * mm});
            skLineSegment(sketch, "E2.16.10.0", {"start": v(107.95, 33.02) * mm, "end": v(111.12, 33.02) * mm});
            skLineSegment(sketch, "E2.16.10.1", {"start": v(111.12, 29.85) * mm, "end": v(111.12, 33.02) * mm});
            skLineSegment(sketch, "E2.16.10.2", {"start": v(107.95, 29.85) * mm, "end": v(111.12, 29.85) * mm});
            skLineSegment(sketch, "E2.16.10.3", {"start": v(107.95, 29.85) * mm, "end": v(107.95, 33.02) * mm});
            skLineSegment(sketch, "E2.16.11.0", {"start": v(107.95, 26.67) * mm, "end": v(111.12, 26.67) * mm});
            skLineSegment(sketch, "E2.16.11.1", {"start": v(111.12, 23.5) * mm, "end": v(111.12, 26.67) * mm});
            skLineSegment(sketch, "E2.16.11.2", {"start": v(107.95, 23.5) * mm, "end": v(111.12, 23.5) * mm});
            skLineSegment(sketch, "E2.16.11.3", {"start": v(107.95, 23.5) * mm, "end": v(107.95, 26.67) * mm});
            skLineSegment(sketch, "E2.16.12.0", {"start": v(107.95, 20.32) * mm, "end": v(111.12, 20.32) * mm});
            skLineSegment(sketch, "E2.16.12.1", {"start": v(111.12, 17.15) * mm, "end": v(111.12, 20.32) * mm});
            skLineSegment(sketch, "E2.16.12.2", {"start": v(107.95, 17.15) * mm, "end": v(111.12, 17.15) * mm});
            skLineSegment(sketch, "E2.16.12.3", {"start": v(107.95, 17.15) * mm, "end": v(107.95, 20.32) * mm});
            skLineSegment(sketch, "E2.16.13.0", {"start": v(107.95, 13.97) * mm, "end": v(111.12, 13.97) * mm});
            skLineSegment(sketch, "E2.16.13.1", {"start": v(111.12, 10.8) * mm, "end": v(111.12, 13.97) * mm});
            skLineSegment(sketch, "E2.16.13.2", {"start": v(107.95, 10.8) * mm, "end": v(111.12, 10.8) * mm});
            skLineSegment(sketch, "E2.16.13.3", {"start": v(107.95, 10.8) * mm, "end": v(107.95, 13.97) * mm});
            skLineSegment(sketch, "E2.16.14.0", {"start": v(107.95, 7.62) * mm, "end": v(111.12, 7.62) * mm});
            skLineSegment(sketch, "E2.16.14.1", {"start": v(111.12, 4.45) * mm, "end": v(111.12, 7.62) * mm});
            skLineSegment(sketch, "E2.16.14.2", {"start": v(107.95, 4.45) * mm, "end": v(111.12, 4.45) * mm});
            skLineSegment(sketch, "E2.16.14.3", {"start": v(107.95, 4.45) * mm, "end": v(107.95, 7.62) * mm});
            skLineSegment(sketch, "E2.direction1", {"start": v(9.52, 117.48) * mm, "end": v(15.87, 117.48) * mm, "construction": true});
            skLineSegment(sketch, "E2.direction2", {"start": v(9.52, 117.48) * mm, "end": v(9.52, 111.13) * mm, "construction": true});
            skLineSegment(sketch, "E3.bottom", {"start": v(118.53, 0) * mm, "end": v(108.37, 0) * mm});
            skLineSegment(sketch, "E3.top", {"start": v(118.53, -6.35) * mm, "end": v(108.37, -6.35) * mm});
            skLineSegment(sketch, "E3.left", {"start": v(118.53, 0) * mm, "end": v(118.53, -6.35) * mm});
            skLineSegment(sketch, "E3.right", {"start": v(108.37, 0) * mm, "end": v(108.37, -6.35) * mm});
            skLineSegment(sketch, "E4.bottom", {"start": v(118.53, 101.6) * mm, "end": v(108.37, 101.6) * mm});
            skLineSegment(sketch, "E4.top", {"start": v(118.53, 107.95) * mm, "end": v(108.37, 107.95) * mm});
            skLineSegment(sketch, "E4.left", {"start": v(118.53, 101.6) * mm, "end": v(118.53, 107.95) * mm});
            skLineSegment(sketch, "E4.right", {"start": v(108.37, 101.6) * mm, "end": v(108.37, 107.95) * mm});
            skLineSegment(sketch, "E5.bottom", {"start": v(0, 101.6) * mm, "end": v(6.35, 101.6) * mm});
            skLineSegment(sketch, "E5.top", {"start": v(0, 107.95) * mm, "end": v(6.35, 107.95) * mm});
            skLineSegment(sketch, "E5.left", {"start": v(0, 101.6) * mm, "end": v(0, 107.95) * mm});
            skLineSegment(sketch, "E5.right", {"start": v(6.35, 101.6) * mm, "end": v(6.35, 107.95) * mm});
            skLineSegment(sketch, "E6.bottom", {"start": v(0, 0) * mm, "end": v(6.35, 0) * mm});
            skLineSegment(sketch, "E6.top", {"start": v(0, -6.35) * mm, "end": v(6.35, -6.35) * mm});
            skLineSegment(sketch, "E6.left", {"start": v(0, 0) * mm, "end": v(0, -6.35) * mm});
            skLineSegment(sketch, "E6.right", {"start": v(6.35, 0) * mm, "end": v(6.35, -6.35) * mm});
            skSolve(sketch);
        }
        {
            var Q0;
            Q0=makeQuery(id+"F1.imprint","IMPRINT",FACE,{"disambiguationData":[TD([[makeQuery(id+"F1.imprint","IMPRINT",EDGE,{"derivedFrom":sQuery(id+"F1.wireOp",EDGE,"E6.bottom")}),-1.0]])]});
            var Q1;
            Q1=makeQuery(id+"F1.imprint","IMPRINT",FACE,{"disambiguationData":[TD([[makeQuery(id+"F1.imprint","IMPRINT",EDGE,{"derivedFrom":sQuery(id+"F1.wireOp",EDGE,"E0.bottom")}),1.0]])]});
            var Q2;
            Q2=makeQuery(id+"F1.imprint","IMPRINT",FACE,{"disambiguationData":[TD([[makeQuery(id+"F1.imprint","IMPRINT",EDGE,{"derivedFrom":sQuery(id+"F1.wireOp",EDGE,"E3.bottom")}),1.0]])]});
            var Q3;
            Q3=makeQuery(id+"F1.imprint","IMPRINT",FACE,{"disambiguationData":[TD([[makeQuery(id+"F1.imprint","IMPRINT",EDGE,{"derivedFrom":sQuery(id+"F1.wireOp",EDGE,"E5.bottom")}),1.0]])]});
            var Q4;
            Q4=makeQuery(id+"F1.imprint","IMPRINT",FACE,{"disambiguationData":[TD([[makeQuery(id+"F1.imprint","IMPRINT",EDGE,{"derivedFrom":sQuery(id+"F1.wireOp",EDGE,"E4.bottom")}),-1.0]])]});
            extrude(context, id + "F2", {"entities" : qUnion([Q0, Q1, Q2, Q3, Q4]), "depth" : getVariable(context, 'thickness')});
        }
    });
